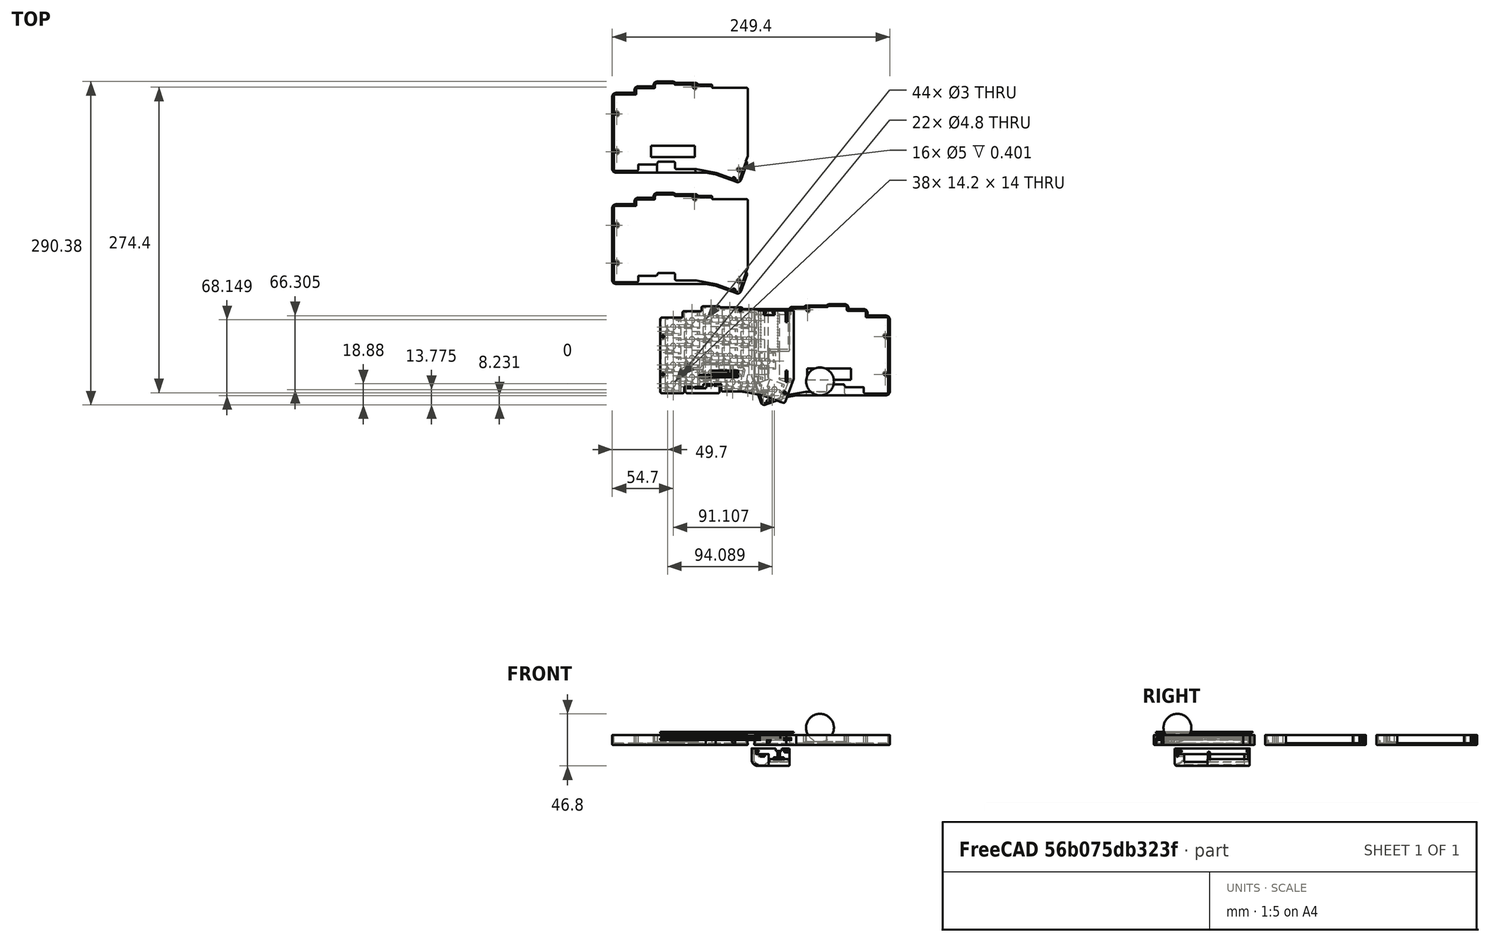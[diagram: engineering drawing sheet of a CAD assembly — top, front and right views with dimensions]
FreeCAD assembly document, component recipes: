
FREECAD ASSEMBLY — COMPONENT RECIPES ("simple-case-xs")

This assembly document has 5 components, labeled P0..P4 below (a component is one placed body or linked part). 4 of them carry a construction recipe — the FreeCAD feature program that regenerates the part from scratch, quoted from this document or its linked companion documents; the rest are supplied as boundary geometry only. No exploded tour is included for this assembly.
NOTE — document 2 of 3 of this assembly tour. The two overview renders and the header above are repeated from document 1; the component sections below continue where the previous document stopped.
COMPONENT P2 — recipe-attached ("case-key001", modeled in this document).
Construction recipe (the document's own serialized feature program — sketch geometry with constraints, then the solid features built on it; lengths are millimeters unless a unit is written):

FEATURE [Sketcher::SketchObject] Sketch020  label="top-plate"
  ArcFitTolerance = 1e-06
  FullyConstrained = true
  MakeInternals = false
  Placement = pos=(0,0,6.6e-15) rot=(0,0,1;0rad)
  sketch-geometry (128):
    g0: ArcOfCircle CenterX=45.3 CenterY=2.4 CenterZ=0 NormalX=-1e-16 NormalY=0 NormalZ=1 AngleXU=1.5708 Radius=1.5 StartAngle=0 EndAngle=1.22777
    g1: LineSegment StartX=59.4 StartY=3.9 StartZ=0 EndX=45.3 EndY=3.9 EndZ=0
    g2: LineSegment StartX=43.8874 StartY=2.9045 StartZ=0 EndX=43.8874 EndY=2.8 EndZ=0
    g3: ArcOfCircle CenterX=59.4 CenterY=2.4 CenterZ=0 NormalX=-1e-16 NormalY=0 NormalZ=1 AngleXU=3.90995e-07 Radius=1.5 StartAngle=0 EndAngle=1.5708
    g4: LineSegment StartX=60.9 StartY=-0.4 StartZ=0 EndX=60.9 EndY=2.4 EndZ=0
    g5: LineSegment StartX=76.4 StartY=-0.4 StartZ=0 EndX=60.9 EndY=-0.4 EndZ=0
    g6: ArcOfCircle CenterX=76.4 CenterY=-1.9 CenterZ=0 NormalX=-1e-16 NormalY=0 NormalZ=1 AngleXU=3.90995e-07 Radius=1.5 StartAngle=0 EndAngle=1.5708
    g7: LineSegment StartX=77.9 StartY=-6.3 StartZ=0 EndX=77.9 EndY=-1.9 EndZ=0
    g8: LineSegment StartX=96.4 StartY=-6.3 StartZ=0 EndX=77.9 EndY=-6.3 EndZ=0
    g9: ArcOfCircle CenterX=96.4 CenterY=-7.8 CenterZ=0 NormalX=-1e-16 NormalY=0 NormalZ=1 AngleXU=3.90995e-07 Radius=1.5 StartAngle=0 EndAngle=1.5708
    g10: LineSegment StartX=97.9 StartY=-59.8 StartZ=0 EndX=97.9 EndY=-7.8 EndZ=0
    g11: LineSegment StartX=97.9 StartY=-72.8 StartZ=0 EndX=97.9 EndY=-59.8 EndZ=0
    g12: ArcOfCircle CenterX=96.4 CenterY=-72.8 CenterZ=0 NormalX=-1e-16 NormalY=0 NormalZ=1 AngleXU=-1.5708 Radius=1.5 StartAngle=0 EndAngle=1.5708
    g13: LineSegment StartX=78 StartY=-74.3 StartZ=0 EndX=96.4 EndY=-74.3 EndZ=0
    g14: ArcOfCircle CenterX=78 CenterY=-72.8 CenterZ=0 NormalX=-1e-16 NormalY=0 NormalZ=1 AngleXU=-3.14159 Radius=1.5 StartAngle=0 EndAngle=1.5708
    g15: LineSegment StartX=76.5 StartY=-68.4 StartZ=0 EndX=76.5 EndY=-72.8 EndZ=0
    g16: LineSegment StartX=60.7 StartY=-68.4 StartZ=0 EndX=76.5 EndY=-68.4 EndZ=0
    g17: ArcOfCircle CenterX=60.7 CenterY=-66.9 CenterZ=0 NormalX=-1e-16 NormalY=0 NormalZ=1 AngleXU=-3.14159 Radius=1.5 StartAngle=0 EndAngle=1.5708
    g18: LineSegment StartX=59.2 StartY=-66.1 StartZ=0 EndX=59.2 EndY=-66.9 EndZ=0
    g19: LineSegment StartX=43.1 StartY=-66.1 StartZ=0 EndX=59.2 EndY=-66.1 EndZ=0
    g20: LineSegment StartX=43.1 StartY=-71.2 StartZ=0 EndX=43.1 EndY=-66.1 EndZ=0
    g21: ArcOfCircle CenterX=41.6 CenterY=-71.2 CenterZ=0 NormalX=-1e-16 NormalY=0 NormalZ=1 AngleXU=-1.5708 Radius=1.5 StartAngle=0 EndAngle=1.5708
    g22: LineSegment StartX=41.4 StartY=-72.7 StartZ=0 EndX=41.6 EndY=-72.7 EndZ=0
    g23: LineSegment StartX=24.227 StartY=-72.7043 StartZ=0 EndX=41.4 EndY=-72.7 EndZ=0
    g24: LineSegment StartX=6.18739 StartY=-75.9853 StartZ=0 EndX=24.227 EndY=-72.7043 EndZ=0
    g25: LineSegment StartX=-12.4977 StartY=-82.7894 StartZ=0 EndX=6.18739 EndY=-75.9853 EndZ=0
    g26: ArcOfCircle CenterX=-13.0109 CenterY=-81.3798 CenterZ=0 NormalX=-1e-16 NormalY=0 NormalZ=1 AngleXU=-2.78723 Radius=1.50005 StartAngle=0 EndAngle=1.56562
    g27: LineSegment StartX=-20.3 StartY=-66 StartZ=0 EndX=-14.4178 EndY=-81.9004 EndZ=0
    g28: LineSegment StartX=-9.1 StartY=-61.9235 StartZ=0 EndX=-20.3 EndY=-66 EndZ=0
    g29: LineSegment StartX=-9.1 StartY=-61 StartZ=0 EndX=-9.1 EndY=-61.9235 EndZ=0
    g30: LineSegment StartX=-9.1 StartY=-36.9 StartZ=0 EndX=-9.1 EndY=-61 EndZ=0
    g31: LineSegment StartX=9.9 StartY=-36.9 StartZ=0 EndX=-9.1 EndY=-36.9 EndZ=0
    g32: LineSegment StartX=9.9 StartY=1.3 StartZ=0 EndX=9.9 EndY=-36.9 EndZ=0
    g33: LineSegment StartX=23.7 StartY=1.3 StartZ=0 EndX=9.9 EndY=1.3 EndZ=0
    g34: ArcOfCircle CenterX=25.2 CenterY=1.3 CenterZ=0 NormalX=-1e-16 NormalY=0 NormalZ=1 AngleXU=1.5708 Radius=1.5 StartAngle=0 EndAngle=1.5708
    g35: LineSegment StartX=43.8874 StartY=2.8 StartZ=0 EndX=25.2 EndY=2.8 EndZ=0
    g36: LineSegment StartX=93.5 StartY=-72.8 StartZ=0 EndX=79.3 EndY=-72.8 EndZ=0
    g37: LineSegment StartX=93.5 StartY=-58.8 StartZ=0 EndX=93.5 EndY=-72.8 EndZ=0
    g38: LineSegment StartX=79.3 StartY=-58.8 StartZ=0 EndX=93.5 EndY=-58.8 EndZ=0
    g39: LineSegment StartX=79.3 StartY=-72.8 StartZ=0 EndX=79.3 EndY=-58.8 EndZ=0
    g40: LineSegment StartX=76.5 StartY=-66.85 StartZ=0 EndX=62.3 EndY=-66.85 EndZ=0
    g41: LineSegment StartX=76.5 StartY=-52.85 StartZ=0 EndX=76.5 EndY=-66.85 EndZ=0
    g42: LineSegment StartX=62.3 StartY=-52.85 StartZ=0 EndX=76.5 EndY=-52.85 EndZ=0
    g43: LineSegment StartX=62.3 StartY=-66.85 StartZ=0 EndX=62.3 EndY=-52.85 EndZ=0
    g44: Circle CenterX=95.6 CenterY=-57.3 CenterZ=0 NormalX=-1e-16 NormalY=0 NormalZ=1 AngleXU=-1.5708 Radius=1.1
    g45: LineSegment StartX=93.5 StartY=-55.8 StartZ=0 EndX=79.3 EndY=-55.8 EndZ=0
    g46: LineSegment StartX=93.5 StartY=-41.8 StartZ=0 EndX=93.5 EndY=-55.8 EndZ=0
    g47: LineSegment StartX=79.3 StartY=-41.8 StartZ=0 EndX=93.5 EndY=-41.8 EndZ=0
    g48: LineSegment StartX=79.3 StartY=-55.8 StartZ=0 EndX=79.3 EndY=-41.8 EndZ=0
    g49: LineSegment StartX=76.5 StartY=-49.85 StartZ=0 EndX=62.3 EndY=-49.85 EndZ=0
    g50: LineSegment StartX=76.5 StartY=-35.85 StartZ=0 EndX=76.5 EndY=-49.85 EndZ=0
    g51: LineSegment StartX=62.3 StartY=-35.85 StartZ=0 EndX=76.5 EndY=-35.85 EndZ=0
    g52: LineSegment StartX=62.3 StartY=-49.85 StartZ=0 EndX=62.3 EndY=-35.85 EndZ=0
    g53: LineSegment StartX=59.5 StartY=-62.6 StartZ=0 EndX=45.3 EndY=-62.6 EndZ=0
    g54: LineSegment StartX=59.5 StartY=-48.6 StartZ=0 EndX=59.5 EndY=-62.6 EndZ=0
    g55: LineSegment StartX=45.3 StartY=-48.6 StartZ=0 EndX=59.5 EndY=-48.6 EndZ=0
    g56: LineSegment StartX=45.3 StartY=-62.6 StartZ=0 EndX=45.3 EndY=-48.6 EndZ=0
    g57: LineSegment StartX=39.95 StartY=-71.1 StartZ=0 EndX=25.75 EndY=-71.1 EndZ=0
    g58: LineSegment StartX=39.95 StartY=-57.1 StartZ=0 EndX=39.95 EndY=-71.1 EndZ=0
    g59: LineSegment StartX=25.75 StartY=-57.1 StartZ=0 EndX=39.95 EndY=-57.1 EndZ=0
    g60: LineSegment StartX=25.75 StartY=-71.1 StartZ=0 EndX=25.75 EndY=-57.1 EndZ=0
    g61: LineSegment StartX=21.8608 StartY=-71.3659 StartZ=0 EndX=7.87653 EndY=-73.8317 EndZ=0
    g62: LineSegment StartX=19.4297 StartY=-57.5786 StartZ=0 EndX=21.8608 EndY=-71.3659 EndZ=0
    g63: LineSegment StartX=5.44545 StartY=-60.0444 StartZ=0 EndX=19.4297 EndY=-57.5786 EndZ=0
    g64: LineSegment StartX=7.87653 StartY=-73.8317 StartZ=0 EndX=5.44545 EndY=-60.0444 EndZ=0
    g65: LineSegment StartX=4.35879 StartY=-75.0546 StartZ=0 EndX=-8.98485 EndY=-79.9113 EndZ=0
    g66: LineSegment StartX=-0.429495 StartY=-61.8989 StartZ=0 EndX=4.35879 EndY=-75.0546 EndZ=0
    g67: LineSegment StartX=-13.7731 StartY=-66.7556 StartZ=0 EndX=-0.429495 EndY=-61.8989 EndZ=0
    g68: LineSegment StartX=-8.98485 StartY=-79.9113 StartZ=0 EndX=-13.7731 EndY=-66.7556 EndZ=0
    g69: Circle CenterX=-14 CenterY=-73.8 CenterZ=0 NormalX=-1e-16 NormalY=0 NormalZ=1 AngleXU=-1.5708 Radius=1.1
    g70: LineSegment StartX=42.5 StartY=-47.725 StartZ=0 EndX=28.3 EndY=-47.725 EndZ=0
    g71: LineSegment StartX=42.5 StartY=-33.725 StartZ=0 EndX=42.5 EndY=-47.725 EndZ=0
    g72: LineSegment StartX=28.3 StartY=-33.725 StartZ=0 EndX=42.5 EndY=-33.725 EndZ=0
    g73: LineSegment StartX=28.3 StartY=-47.725 StartZ=0 EndX=28.3 EndY=-33.725 EndZ=0
    g74: LineSegment StartX=25.5 StartY=-49.85 StartZ=0 EndX=11.3 EndY=-49.85 EndZ=0
    g75: LineSegment StartX=25.5 StartY=-35.85 StartZ=0 EndX=25.5 EndY=-49.85 EndZ=0
    g76: LineSegment StartX=11.3 StartY=-35.85 StartZ=0 EndX=25.5 EndY=-35.85 EndZ=0
    g77: LineSegment StartX=11.3 StartY=-49.85 StartZ=0 EndX=11.3 EndY=-35.85 EndZ=0
    g78: LineSegment StartX=8.5 StartY=-52.4 StartZ=0 EndX=-5.7 EndY=-52.4 EndZ=0
    g79: LineSegment StartX=8.5 StartY=-38.4 StartZ=0 EndX=8.5 EndY=-52.4 EndZ=0
    g80: LineSegment StartX=-5.7 StartY=-38.4 StartZ=0 EndX=8.5 EndY=-38.4 EndZ=0
    g81: LineSegment StartX=-5.7 StartY=-52.4 StartZ=0 EndX=-5.7 EndY=-38.4 EndZ=0
    g82: LineSegment StartX=93.5 StartY=-38.8 StartZ=0 EndX=79.3 EndY=-38.8 EndZ=0
    g83: LineSegment StartX=93.5 StartY=-24.8 StartZ=0 EndX=93.5 EndY=-38.8 EndZ=0
    g84: LineSegment StartX=79.3 StartY=-24.8 StartZ=0 EndX=93.5 EndY=-24.8 EndZ=0
    g85: LineSegment StartX=79.3 StartY=-38.8 StartZ=0 EndX=79.3 EndY=-24.8 EndZ=0
    g86: Circle CenterX=95.6 CenterY=-23.3 CenterZ=0 NormalX=-1e-16 NormalY=0 NormalZ=1 AngleXU=-1.5708 Radius=1.1
    g87: LineSegment StartX=76.5 StartY=-32.85 StartZ=0 EndX=62.3 EndY=-32.85 EndZ=0
    g88: LineSegment StartX=76.5 StartY=-18.85 StartZ=0 EndX=76.5 EndY=-32.85 EndZ=0
    g89: LineSegment StartX=62.3 StartY=-18.85 StartZ=0 EndX=76.5 EndY=-18.85 EndZ=0
    g90: LineSegment StartX=62.3 StartY=-32.85 StartZ=0 EndX=62.3 EndY=-18.85 EndZ=0
    g91: LineSegment StartX=59.5 StartY=-45.6 StartZ=0 EndX=45.3 EndY=-45.6 EndZ=0
    g92: LineSegment StartX=59.5 StartY=-31.6 StartZ=0 EndX=59.5 EndY=-45.6 EndZ=0
    g93: LineSegment StartX=45.3 StartY=-31.6 StartZ=0 EndX=59.5 EndY=-31.6 EndZ=0
    g94: LineSegment StartX=45.3 StartY=-45.6 StartZ=0 EndX=45.3 EndY=-31.6 EndZ=0
    g95: LineSegment StartX=59.5 StartY=-28.6 StartZ=0 EndX=45.3 EndY=-28.6 EndZ=0
    g96: LineSegment StartX=59.5 StartY=-14.6 StartZ=0 EndX=59.5 EndY=-28.6 EndZ=0
    g97: LineSegment StartX=45.3 StartY=-14.6 StartZ=0 EndX=59.5 EndY=-14.6 EndZ=0
    g98: LineSegment StartX=45.3 StartY=-28.6 StartZ=0 EndX=45.3 EndY=-14.6 EndZ=0
    g99: LineSegment StartX=93.5 StartY=-21.8 StartZ=0 EndX=79.3 EndY=-21.8 EndZ=0
    g100: LineSegment StartX=93.5 StartY=-7.8 StartZ=0 EndX=93.5 EndY=-21.8 EndZ=0
    g101: LineSegment StartX=79.3 StartY=-7.8 StartZ=0 EndX=93.5 EndY=-7.8 EndZ=0
    g102: LineSegment StartX=79.3 StartY=-21.8 StartZ=0 EndX=79.3 EndY=-7.8 EndZ=0
    g103: LineSegment StartX=76.5 StartY=-15.85 StartZ=0 EndX=62.3 EndY=-15.85 EndZ=0
    g104: LineSegment StartX=76.5 StartY=-1.85 StartZ=0 EndX=76.5 EndY=-15.85 EndZ=0
    g105: LineSegment StartX=62.3 StartY=-1.85 StartZ=0 EndX=76.5 EndY=-1.85 EndZ=0
    g106: LineSegment StartX=62.3 StartY=-15.85 StartZ=0 EndX=62.3 EndY=-1.85 EndZ=0
    g107: LineSegment StartX=59.5 StartY=-11.6 StartZ=0 EndX=45.3 EndY=-11.6 EndZ=0
    g108: LineSegment StartX=59.5 StartY=2.4 StartZ=0 EndX=59.5 EndY=-11.6 EndZ=0
    g109: LineSegment StartX=45.3 StartY=2.4 StartZ=0 EndX=59.5 EndY=2.4 EndZ=0
    g110: LineSegment StartX=45.3 StartY=-11.6 StartZ=0 EndX=45.3 EndY=2.4 EndZ=0
    g111: LineSegment StartX=42.5 StartY=-30.725 StartZ=0 EndX=28.3 EndY=-30.725 EndZ=0
    g112: LineSegment StartX=42.5 StartY=-16.725 StartZ=0 EndX=42.5 EndY=-30.725 EndZ=0
    g113: LineSegment StartX=28.3 StartY=-16.725 StartZ=0 EndX=42.5 EndY=-16.725 EndZ=0
    g114: LineSegment StartX=28.3 StartY=-30.725 StartZ=0 EndX=28.3 EndY=-16.725 EndZ=0
    g115: LineSegment StartX=25.5 StartY=-32.85 StartZ=0 EndX=11.3 EndY=-32.85 EndZ=0
    g116: LineSegment StartX=25.5 StartY=-18.85 StartZ=0 EndX=25.5 EndY=-32.85 EndZ=0
    g117: LineSegment StartX=11.3 StartY=-18.85 StartZ=0 EndX=25.5 EndY=-18.85 EndZ=0
    g118: LineSegment StartX=11.3 StartY=-32.85 StartZ=0 EndX=11.3 EndY=-18.85 EndZ=0
    g119: LineSegment StartX=25.5 StartY=-15.85 StartZ=0 EndX=11.3 EndY=-15.85 EndZ=0
    g120: LineSegment StartX=25.5 StartY=-1.85 StartZ=0 EndX=25.5 EndY=-15.85 EndZ=0
    g121: LineSegment StartX=11.3 StartY=-1.85 StartZ=0 EndX=25.5 EndY=-1.85 EndZ=0
    g122: LineSegment StartX=11.3 StartY=-15.85 StartZ=0 EndX=11.3 EndY=-1.85 EndZ=0
    g123: LineSegment StartX=42.5 StartY=-13.725 StartZ=0 EndX=28.3 EndY=-13.725 EndZ=0
    g124: LineSegment StartX=42.5 StartY=0.275 StartZ=0 EndX=42.5 EndY=-13.725 EndZ=0
    g125: LineSegment StartX=28.3 StartY=0.275 StartZ=0 EndX=42.5 EndY=0.275 EndZ=0
    g126: LineSegment StartX=28.3 StartY=-13.725 StartZ=0 EndX=28.3 EndY=0.275 EndZ=0
    g127: Circle CenterX=25.9 CenterY=0.6 CenterZ=0 NormalX=-1e-16 NormalY=0 NormalZ=1 AngleXU=-1.5708 Radius=1.1
  constraints (252):
    c: Block(g0)
    c: Block(g1)
    c: Block(g2)
    c: Block(g3)
    c: Block(g4)
    c: Block(g5)
    c: Block(g6)
    c: Block(g7)
    c: Block(g8)
    c: Block(g9)
    c: Block(g10)
    c: Block(g11)
    c: Block(g12)
    c: Block(g13)
    c: Block(g14)
    c: Block(g15)
    c: Block(g16)
    c: Block(g17)
    c: Block(g18)
    c: Block(g19)
    c: Block(g20)
    c: Block(g21)
    c: Block(g22)
    c: Block(g23)
    c: Block(g24)
    c: Block(g25)
    c: Block(g26)
    c: Block(g27)
    c: Block(g28)
    c: Block(g29)
    c: Block(g30)
    c: Block(g31)
    c: Block(g32)
    c: Block(g33)
    c: Block(g34)
    c: Block(g35)
    c: Block(g36)
    c: Block(g37)
    c: Block(g38)
    c: Block(g39)
    c: Block(g40)
    c: Block(g41)
    c: Block(g42)
    c: Block(g43)
    c: Block(g44)
    c: Block(g45)
    c: Block(g46)
    c: Block(g47)
    c: Block(g48)
    c: Block(g49)
    c: Block(g50)
    c: Block(g51)
    c: Block(g52)
    c: Block(g53)
    c: Block(g54)
    c: Block(g55)
    c: Block(g56)
    c: Block(g57)
    c: Block(g58)
    c: Block(g59)
    c: Block(g60)
    c: Block(g61)
    c: Block(g62)
    c: Block(g63)
    c: Block(g64)
    c: Block(g65)
    c: Block(g66)
    c: Block(g67)
    c: Block(g68)
    c: Block(g69)
    c: Block(g70)
    c: Block(g71)
    c: Block(g72)
    c: Block(g73)
    c: Block(g74)
    c: Block(g75)
    c: Block(g76)
    c: Block(g77)
    c: Block(g78)
    c: Block(g79)
    c: Block(g80)
    c: Block(g81)
    c: Block(g82)
    c: Block(g83)
    c: Block(g84)
    c: Block(g85)
    c: Block(g86)
    c: Block(g87)
    c: Block(g88)
    c: Block(g89)
    c: Block(g90)
    c: Block(g91)
    c: Block(g92)
    c: Block(g93)
    c: Block(g94)
    c: Block(g95)
    c: Block(g96)
    c: Block(g97)
    c: Block(g98)
    c: Block(g99)
    c: Block(g100)
    c: Block(g101)
    c: Block(g102)
    c: Block(g103)
    c: Block(g104)
    c: Block(g105)
    c: Block(g106)
    c: Block(g107)
    c: Block(g108)
    c: Block(g109)
    c: Block(g110)
    c: Block(g111)
    c: Block(g112)
    c: Block(g113)
    c: Block(g114)
    c: Block(g115)
    c: Block(g116)
    c: Block(g117)
    c: Block(g118)
    c: Block(g119)
    c: Block(g120)
    c: Block(g121)
    c: Block(g122)
    c: Block(g123)
    c: Block(g124)
    c: Block(g125)
    c: Block(g126)
    c: Block(g127)
    c: Coincident(g27,g28)
    c: Coincident(g26,g27)
    c: Coincident(g67,g68)
    c: Coincident(g25,g26)
    c: Coincident(g28,g29)
    c: Coincident(g29,g30)
    c: Coincident(g30,g31)
    c: Coincident(g65,g68)
    c: Coincident(g78,g81)
    c: Coincident(g80,g81)
    c: Coincident(g66,g67)
    c: Coincident(g65,g66)
    c: Coincident(g63,g64)
    c: Coincident(g24,g25)
    c: Coincident(g61,g64)
    c: Coincident(g78,g79)
    c: Coincident(g79,g80)
    c: Coincident(g31,g32)
    c: Coincident(g32,g33)
    c: Coincident(g74,g77)
    c: Coincident(g76,g77)
    c: Coincident(g115,g118)
    c: Coincident(g117,g118)
    c: Coincident(g119,g122)
    c: Coincident(g121,g122)
    c: Coincident(g62,g63)
    c: Coincident(g61,g62)
    c: Coincident(g33,g34)
    c: Coincident(g23,g24)
    c: Coincident(g34,g35)
    c: Coincident(g74,g75)
    c: Coincident(g75,g76)
    c: Coincident(g115,g116)
    c: Coincident(g116,g117)
    c: Coincident(g119,g120)
    c: Coincident(g120,g121)
    c: Coincident(g57,g60)
    c: Coincident(g59,g60)
    c: Coincident(g70,g73)
    c: Coincident(g72,g73)
    c: Coincident(g111,g114)
    c: Coincident(g113,g114)
    c: Coincident(g123,g126)
    c: Coincident(g125,g126)
    c: Coincident(g57,g58)
    c: Coincident(g58,g59)
    c: Coincident(g22,g23)
    c: Coincident(g21,g22)
    c: Coincident(g70,g71)
    c: Coincident(g71,g72)
    c: Coincident(g111,g112)
    c: Coincident(g112,g113)
    c: Coincident(g123,g124)
    c: Coincident(g124,g125)
    c: Coincident(g20,g21)
    c: Coincident(g19,g20)
    c: Coincident(g2,g35)
    c: Coincident(g0,g2)
    c: Coincident(g53,g56)
    c: Coincident(g55,g56)
    c: Coincident(g91,g94)
    c: Coincident(g93,g94)
    c: Coincident(g95,g98)
    c: Coincident(g97,g98)
    c: Coincident(g107,g110)
    c: Coincident(g109,g110)
    c: Coincident(g0,g1)
    c: Coincident(g17,g18)
    c: Coincident(g18,g19)
    c: Coincident(g1,g3)
    c: Coincident(g53,g54)
    c: Coincident(g54,g55)
    c: Coincident(g91,g92)
    c: Coincident(g92,g93)
    c: Coincident(g95,g96)
    c: Coincident(g96,g97)
    c: Coincident(g107,g108)
    c: Coincident(g108,g109)
    c: Coincident(g16,g17)
    c: Coincident(g4,g5)
    c: Coincident(g3,g4)
    c: Coincident(g40,g43)
    c: Coincident(g42,g43)
    c: Coincident(g49,g52)
    c: Coincident(g51,g52)
    c: Coincident(g87,g90)
    c: Coincident(g89,g90)
    c: Coincident(g103,g106)
    c: Coincident(g105,g106)
    c: Coincident(g5,g6)
    c: Coincident(g14,g15)
    c: Coincident(g15,g16)
    c: Coincident(g40,g41)
    c: Coincident(g41,g42)
    c: Coincident(g49,g50)
    c: Coincident(g50,g51)
    c: Coincident(g87,g88)
    c: Coincident(g88,g89)
    c: Coincident(g103,g104)
    c: Coincident(g104,g105)
    c: Coincident(g7,g8)
    c: Coincident(g6,g7)
    c: Coincident(g13,g14)
    c: Coincident(g36,g39)
    c: Coincident(g38,g39)
    c: Coincident(g45,g48)
    c: Coincident(g47,g48)
    c: Coincident(g82,g85)
    c: Coincident(g84,g85)
    c: Coincident(g99,g102)
    c: Coincident(g101,g102)
    c: Coincident(g36,g37)
    c: Coincident(g37,g38)
    c: Coincident(g45,g46)
    c: Coincident(g46,g47)
    c: Coincident(g82,g83)
    c: Coincident(g83,g84)
    c: Coincident(g99,g100)
    c: Coincident(g100,g101)
    c: Coincident(g12,g13)
    c: Coincident(g8,g9)
    c: Coincident(g11,g12)
    c: Coincident(g10,g11)
    c: Coincident(g9,g10)
FEATURE [Sketcher::SketchObject] Sketch021
  ArcFitTolerance = 1e-06
  AttachmentOffset = pos=(0,0,-5.1) rot=(0,0,1;0rad)
  AttachmentSupport = -> [XY_Plane004]
  FullyConstrained = false
  MakeInternals = false
  MapMode = 5
  Placement = pos=(0,0,-5.1) rot=(0,0,1;0rad)
  sketch-geometry (61):
    g0: ArcOfCircle [constr] CenterX=45.3 CenterY=2.4 CenterZ=0 NormalX=-1e-16 NormalY=0 NormalZ=1 AngleXU=1.5708 Radius=1.5 StartAngle=0 EndAngle=1.22777
    g1: LineSegment [constr] StartX=59.4 StartY=3.9 StartZ=0 EndX=45.3 EndY=3.9 EndZ=0
    g2: LineSegment [constr] StartX=43.8874 StartY=2.9045 StartZ=0 EndX=43.8874 EndY=2.8 EndZ=0
    g3: ArcOfCircle [constr] CenterX=59.4 CenterY=2.4 CenterZ=0 NormalX=-1e-16 NormalY=0 NormalZ=1 AngleXU=3.90995e-07 Radius=1.5 StartAngle=0 EndAngle=1.5708
    g4: LineSegment [constr] StartX=60.9 StartY=-0.4 StartZ=0 EndX=60.9 EndY=2.4 EndZ=0
    g5: LineSegment [constr] StartX=76.4 StartY=-0.4 StartZ=0 EndX=60.9 EndY=-0.4 EndZ=0
    g6: ArcOfCircle [constr] CenterX=76.4 CenterY=-1.9 CenterZ=0 NormalX=-1e-16 NormalY=0 NormalZ=1 AngleXU=3.90995e-07 Radius=1.5 StartAngle=0 EndAngle=1.5708
    g7: LineSegment [constr] StartX=77.9 StartY=-6.3 StartZ=0 EndX=77.9 EndY=-1.9 EndZ=0
    g8: LineSegment [constr] StartX=96.4 StartY=-6.3 StartZ=0 EndX=77.9 EndY=-6.3 EndZ=0
    g9: ArcOfCircle [constr] CenterX=96.4 CenterY=-7.8 CenterZ=0 NormalX=-1e-16 NormalY=0 NormalZ=1 AngleXU=3.90995e-07 Radius=1.5 StartAngle=0 EndAngle=1.5708
    g10: LineSegment [constr] StartX=97.9 StartY=-59.8 StartZ=0 EndX=97.9 EndY=-7.8 EndZ=0
    g11: LineSegment [constr] StartX=97.9 StartY=-72.8 StartZ=0 EndX=97.9 EndY=-59.8 EndZ=0
    g12: ArcOfCircle [constr] CenterX=96.4 CenterY=-72.8 CenterZ=0 NormalX=-1e-16 NormalY=0 NormalZ=1 AngleXU=-1.5708 Radius=1.5 StartAngle=0 EndAngle=1.5708
    g13: LineSegment [constr] StartX=78 StartY=-74.3 StartZ=0 EndX=96.4 EndY=-74.3 EndZ=0
    g14: LineSegment [constr] StartX=6.18739 StartY=-75.9853 StartZ=0 EndX=15.4535 EndY=-74.3 EndZ=0
    g15: LineSegment [constr] StartX=-12.4977 StartY=-82.7894 StartZ=0 EndX=6.18739 EndY=-75.9853 EndZ=0
    g16: ArcOfCircle [constr] CenterX=-13.0109 CenterY=-81.3798 CenterZ=0 NormalX=-1e-16 NormalY=0 NormalZ=1 AngleXU=-2.78723 Radius=1.50005 StartAngle=0 EndAngle=1.56562
    g17: LineSegment [constr] StartX=-20.3 StartY=-66 StartZ=0 EndX=-14.4178 EndY=-81.9004 EndZ=0
    g18: LineSegment [constr] StartX=-9.1 StartY=-61.9235 StartZ=0 EndX=-20.3 EndY=-66 EndZ=0
    g19: LineSegment [constr] StartX=-9.1 StartY=-61 StartZ=0 EndX=-9.1 EndY=-61.9235 EndZ=0
    g20: LineSegment [constr] StartX=-9.1 StartY=-36.9 StartZ=0 EndX=-9.1 EndY=-61 EndZ=0
    g21: LineSegment [constr] StartX=9.9 StartY=-36.9 StartZ=0 EndX=-9.1 EndY=-36.9 EndZ=0
    g22: LineSegment [constr] StartX=9.9 StartY=1.3 StartZ=0 EndX=9.9 EndY=-36.9 EndZ=0
    g23: LineSegment [constr] StartX=23.7 StartY=1.3 StartZ=0 EndX=9.9 EndY=1.3 EndZ=0
    g24: ArcOfCircle [constr] CenterX=25.2 CenterY=1.3 CenterZ=0 NormalX=-1e-16 NormalY=0 NormalZ=1 AngleXU=1.5708 Radius=1.5 StartAngle=0 EndAngle=1.5708
    g25: LineSegment [constr] StartX=43.8874 StartY=2.8 StartZ=0 EndX=25.2 EndY=2.8 EndZ=0
    g26: LineSegment [constr] StartX=78 StartY=-74.3 StartZ=0 EndX=15.4535 EndY=-74.3 EndZ=0
    g27: LineSegment StartX=78 StartY=-76.1 StartZ=0 EndX=15.6159 EndY=-76.1 EndZ=0
    g28: LineSegment StartX=6.65976 StartY=-77.7289 StartZ=0 EndX=15.6159 EndY=-76.1 EndZ=0
    g29: LineSegment StartX=-11.8818 StartY=-84.4807 StartZ=0 EndX=6.65976 EndY=-77.7289 EndZ=0
    g30: ArcOfCircle CenterX=-13.0109 CenterY=-81.3798 CenterZ=0 NormalX=0 NormalY=0 NormalZ=1 AngleXU=-2.78723 Radius=3.30007 StartAngle=6.28318 EndAngle=7.84881
    g31: LineSegment StartX=-21.9882 StartY=-66.6245 StartZ=0 EndX=-16.106 EndY=-82.5249 EndZ=0
    g32: LineSegment [constr] StartX=-10.9 StartY=-60.6632 StartZ=0 EndX=-20.9156 EndY=-64.3086 EndZ=0
    g33: LineSegment [constr] StartX=-10.9 StartY=-36.9 StartZ=0 EndX=-10.9 EndY=-60.6632 EndZ=0
    g34: ArcOfCircle [constr] CenterX=-9.1 CenterY=-36.9 CenterZ=0 NormalX=0 NormalY=0 NormalZ=1 AngleXU=0 Radius=1.8 StartAngle=1.5708 EndAngle=3.14159
    g35: LineSegment [constr] StartX=8.1 StartY=-35.1 StartZ=0 EndX=-9.1 EndY=-35.1 EndZ=0
    g36: LineSegment [constr] StartX=8.1 StartY=1.3 StartZ=0 EndX=8.1 EndY=-35.1 EndZ=0
    g37: ArcOfCircle [constr] CenterX=9.9 CenterY=1.3 CenterZ=0 NormalX=0 NormalY=0 NormalZ=1 AngleXU=0 Radius=1.8 StartAngle=1.5708 EndAngle=3.14159
    g38: LineSegment [constr] StartX=22.4341 StartY=3.1 StartZ=0 EndX=9.9 EndY=3.1 EndZ=0
    g39: ArcOfCircle CenterX=25.2 CenterY=1.3 CenterZ=0 NormalX=0 NormalY=0 NormalZ=1 AngleXU=1.5708 Radius=3.3 StartAngle=0 EndAngle=0.993864
    g40: LineSegment StartX=42.8403 StartY=4.6 StartZ=0 EndX=25.2 EndY=4.6 EndZ=0
    g41: ArcOfCircle CenterX=45.3 CenterY=2.4 CenterZ=0 NormalX=0 NormalY=0 NormalZ=1 AngleXU=1.5708 Radius=3.3 StartAngle=0 EndAngle=0.841069
    g42: LineSegment StartX=59.4 StartY=5.7 StartZ=0 EndX=45.3 EndY=5.7 EndZ=0
    g43: ArcOfCircle CenterX=59.4 CenterY=2.4 CenterZ=0 NormalX=0 NormalY=0 NormalZ=1 AngleXU=3.90995e-07 Radius=3.3 StartAngle=-1.8e-15 EndAngle=1.5708
    g44: LineSegment StartX=62.7 StartY=1.4 StartZ=0 EndX=62.7 EndY=2.4 EndZ=0
    g45: LineSegment StartX=76.4 StartY=1.4 StartZ=0 EndX=62.7 EndY=1.4 EndZ=0
    g46: ArcOfCircle CenterX=76.4 CenterY=-1.9 CenterZ=0 NormalX=0 NormalY=0 NormalZ=1 AngleXU=3.90995e-07 Radius=3.3 StartAngle=-1.8e-15 EndAngle=1.5708
    g47: LineSegment StartX=79.7 StartY=-4.5 StartZ=0 EndX=79.7 EndY=-1.9 EndZ=0
    g48: LineSegment StartX=96.4 StartY=-4.5 StartZ=0 EndX=79.7 EndY=-4.5 EndZ=0
    g49: ArcOfCircle CenterX=96.4 CenterY=-7.8 CenterZ=0 NormalX=0 NormalY=0 NormalZ=1 AngleXU=3.90995e-07 Radius=3.3 StartAngle=-1.8e-15 EndAngle=1.5708
    g50: LineSegment StartX=99.7 StartY=-59.8 StartZ=0 EndX=99.7 EndY=-7.8 EndZ=0
    g51: LineSegment StartX=99.7 StartY=-72.8 StartZ=0 EndX=99.7 EndY=-59.8 EndZ=0
    g52: ArcOfCircle CenterX=96.4 CenterY=-72.8 CenterZ=0 NormalX=0 NormalY=0 NormalZ=1 AngleXU=-1.5708 Radius=3.3 StartAngle=0 EndAngle=1.5708
    g53: LineSegment StartX=78 StartY=-76.1 StartZ=0 EndX=96.4 EndY=-76.1 EndZ=0
    g54: LineSegment [constr] StartX=8.1 StartY=1.3 StartZ=0 EndX=8.1 EndY=0 EndZ=0
    g55: LineSegment StartX=8.1 StartY=0 StartZ=0 EndX=-22.1 EndY=0 EndZ=0
    g56: LineSegment StartX=-22.1 StartY=0 StartZ=0 EndX=-22.1 EndY=-61.0545 EndZ=0
    g57: LineSegment StartX=-22.1 StartY=-61.0545 StartZ=0 EndX=-20.3 EndY=-66 EndZ=0
    g58: LineSegment StartX=-20.3 StartY=-66 StartZ=0 EndX=-21.9882 EndY=-66.6245 EndZ=0
    g59: LineSegment StartX=22.4341 StartY=3.1 StartZ=0 EndX=8.1 EndY=3.1 EndZ=0
    g60: LineSegment StartX=8.1 StartY=3.1 StartZ=0 EndX=8.1 EndY=0 EndZ=0
  constraints (101):
    c: Block(g0)
    c: Block(g1)
    c: Block(g2)
    c: Block(g3)
    c: Block(g4)
    c: Block(g5)
    c: Block(g6)
    c: Block(g7)
    c: Block(g8)
    c: Block(g9)
    c: Block(g10)
    c: Block(g11)
    c: Block(g12)
    c: Block(g13)
    c: Block(g14)
    c: Block(g15)
    c: Block(g16)
    c: Block(g17)
    c: Block(g18)
    c: Block(g19)
    c: Block(g20)
    c: Block(g21)
    c: Block(g22)
    c: Block(g23)
    c: Block(g24)
    c: Block(g25)
    c: Coincident(g17,g18)
    c: Coincident(g16,g17)
    c: Coincident(g15,g16)
    c: Coincident(g18,g19)
    c: Coincident(g19,g20)
    c: Coincident(g20,g21)
    c: Coincident(g14,g15)
    c: Coincident(g21,g22)
    c: Coincident(g22,g23)
    c: Coincident(g23,g24)
    c: Coincident(g24,g25)
    c: Coincident(g2,g25)
    c: Coincident(g0,g2)
    c: Coincident(g0,g1)
    c: Coincident(g1,g3)
    c: Coincident(g4,g5)
    c: Coincident(g3,g4)
    c: Coincident(g5,g6)
    c: Coincident(g7,g8)
    c: Coincident(g6,g7)
    c: Coincident(g12,g13)
    c: Coincident(g8,g9)
    c: Coincident(g11,g12)
    c: Coincident(g10,g11)
    c: Coincident(g9,g10)
    c: Coincident(g26,g13)
    c: Horizontal(g26)
    c: Coincident(g14,g26)
    c: Coincident(g27,g28)
    c: Coincident(g27,g53)
    c: Coincident(g28,g29)
    c: Coincident(g32,g33)
    c: Tangent(g33,g34) = -1.5708
    c: Tangent(g34,g35) = -1.5708
    c: Coincident(g35,g36)
    c: Tangent(g36,g37) = -1.5708
    c: Tangent(g37,g38) = -1.5708
    c: Coincident(g38,g39)
    c: Coincident(g40,g41)
    c: Coincident(g44,g45)
    c: Coincident(g47,g48)
    c: Coincident(g50,g51)
    c: Coincident(g54,g36)
    c: PointOnObject(g54,g-1)
    c: Vertical(g54)
    c: Coincident(g55,g54)
    c: PointOnObject(g55,g-1)
    c: Coincident(g56,g55)
    c: Vertical(g56)
    c: DistanceX(g55,g-1) = 22.1
    c: Coincident(g57,g56)
    c: Coincident(g57,g17)
    c: Angle(g18,g57) = 1.5708
    c: Coincident(g58,g17)
    c: Coincident(g58,g31)
    c: Coincident(g30,g31)
    c: Coincident(g29,g30)
    c: Coincident(g39,g40)
    c: Coincident(g41,g42)
    c: Coincident(g42,g43)
    c: Coincident(g43,g44)
    c: Coincident(g45,g46)
    c: Coincident(g46,g47)
    c: Coincident(g52,g53)
    c: Coincident(g48,g49)
    c: Coincident(g51,g52)
    c: Coincident(g49,g50)
    c: Block(g38)
    c: Block(g36)
    c: Coincident(g59,g38)
    c: Horizontal(g59)
    c: Tangent(g59,g37)
    c: Coincident(g60,g59)
    c: Coincident(g60,g54)
    c: Vertical(g60)
FEATURE [PartDesign::Pad] Pad010
  Direction = (0,0,1)
  Length = 7.3
  Length2 = 1.5
  Profile = -> Sketch021
  ReferenceAxis = -> Sketch021 [N_Axis]
  Refine = true
  Suppressed = false
  Type = 4
FEATURE [Sketcher::SketchObject] Sketch022  label="bottom-plate"
  ArcFitTolerance = 1e-06
  FullyConstrained = true
  MakeInternals = false
  Placement = pos=(0,0,6.6e-15) rot=(0,0,1;0rad)
  sketch-geometry (74):
    g0: ArcOfCircle CenterX=45.3 CenterY=2.4 CenterZ=0 NormalX=-1e-16 NormalY=0 NormalZ=1 AngleXU=1.5708 Radius=1.5 StartAngle=0 EndAngle=1.22777
    g1: LineSegment StartX=59.4 StartY=3.9 StartZ=0 EndX=45.3 EndY=3.9 EndZ=0
    g2: LineSegment StartX=43.8874 StartY=2.9045 StartZ=0 EndX=43.8874 EndY=2.8 EndZ=0
    g3: ArcOfCircle CenterX=59.4 CenterY=2.4 CenterZ=0 NormalX=-1e-16 NormalY=0 NormalZ=1 AngleXU=3.90995e-07 Radius=1.5 StartAngle=0 EndAngle=1.5708
    g4: LineSegment StartX=60.9 StartY=-0.4 StartZ=0 EndX=60.9 EndY=2.4 EndZ=0
    g5: LineSegment StartX=76.4 StartY=-0.4 StartZ=0 EndX=60.9 EndY=-0.4 EndZ=0
    g6: ArcOfCircle CenterX=76.4 CenterY=-1.9 CenterZ=0 NormalX=-1e-16 NormalY=0 NormalZ=1 AngleXU=3.90995e-07 Radius=1.5 StartAngle=0 EndAngle=1.5708
    g7: LineSegment StartX=77.9 StartY=-6.3 StartZ=0 EndX=77.9 EndY=-1.9 EndZ=0
    g8: LineSegment StartX=96.4 StartY=-6.3 StartZ=0 EndX=77.9 EndY=-6.3 EndZ=0
    g9: ArcOfCircle CenterX=96.4 CenterY=-7.8 CenterZ=0 NormalX=-1e-16 NormalY=0 NormalZ=1 AngleXU=3.90995e-07 Radius=1.5 StartAngle=0 EndAngle=1.5708
    g10: LineSegment StartX=97.9 StartY=-59.8 StartZ=0 EndX=97.9 EndY=-7.8 EndZ=0
    g11: LineSegment StartX=97.9 StartY=-72.8 StartZ=0 EndX=97.9 EndY=-59.8 EndZ=0
    g12: ArcOfCircle CenterX=96.4 CenterY=-72.8 CenterZ=0 NormalX=-1e-16 NormalY=0 NormalZ=1 AngleXU=-1.5708 Radius=1.5 StartAngle=0 EndAngle=1.5708
    g13: LineSegment StartX=78 StartY=-74.3 StartZ=0 EndX=96.4 EndY=-74.3 EndZ=0
    g14: ArcOfCircle CenterX=78 CenterY=-72.8 CenterZ=0 NormalX=-1e-16 NormalY=0 NormalZ=1 AngleXU=-3.14159 Radius=1.5 StartAngle=0 EndAngle=1.5708
    g15: LineSegment StartX=76.5 StartY=-68.4 StartZ=0 EndX=76.5 EndY=-72.8 EndZ=0
    g16: LineSegment StartX=68.6 StartY=-68.4 StartZ=0 EndX=76.5 EndY=-68.4 EndZ=0
    g17: LineSegment StartX=68.6 StartY=-69.9 StartZ=0 EndX=68.6 EndY=-68.4 EndZ=0
    g18: LineSegment StartX=75 StartY=-69.9 StartZ=0 EndX=68.6 EndY=-69.9 EndZ=0
    g19: LineSegment StartX=75 StartY=-72.8 StartZ=0 EndX=75 EndY=-69.9 EndZ=0
    g20: ArcOfCircle CenterX=73.5 CenterY=-72.8 CenterZ=0 NormalX=-1e-16 NormalY=0 NormalZ=1 AngleXU=-1.5708 Radius=1.5 StartAngle=0 EndAngle=1.5708
    g21: LineSegment StartX=46.1 StartY=-74.3 StartZ=0 EndX=73.5 EndY=-74.3 EndZ=0
    g22: ArcOfCircle CenterX=46.1 CenterY=-72.8 CenterZ=0 NormalX=-1e-16 NormalY=0 NormalZ=1 AngleXU=-3.14159 Radius=1.5 StartAngle=0 EndAngle=1.5708
    g23: LineSegment StartX=44.6 StartY=-67.6 StartZ=0 EndX=44.6 EndY=-72.8 EndZ=0
    g24: LineSegment StartX=49.65 StartY=-67.6 StartZ=0 EndX=44.6 EndY=-67.6 EndZ=0
    g25: LineSegment StartX=49.65 StartY=-66.1 StartZ=0 EndX=49.65 EndY=-67.6 EndZ=0
    g26: LineSegment StartX=43.1 StartY=-66.1 StartZ=0 EndX=49.65 EndY=-66.1 EndZ=0
    g27: LineSegment StartX=43.1 StartY=-71.2 StartZ=0 EndX=43.1 EndY=-66.1 EndZ=0
    g28: ArcOfCircle CenterX=41.6 CenterY=-71.2 CenterZ=0 NormalX=-1e-16 NormalY=0 NormalZ=1 AngleXU=-1.5708 Radius=1.5 StartAngle=0 EndAngle=1.5708
    g29: LineSegment StartX=41.4 StartY=-72.7 StartZ=0 EndX=41.6 EndY=-72.7 EndZ=0
    g30: LineSegment StartX=24.227 StartY=-72.7043 StartZ=0 EndX=41.4 EndY=-72.7 EndZ=0
    g31: LineSegment StartX=6.18739 StartY=-75.9853 StartZ=0 EndX=24.227 EndY=-72.7043 EndZ=0
    g32: LineSegment StartX=-12.4977 StartY=-82.7894 StartZ=0 EndX=6.18739 EndY=-75.9853 EndZ=0
    g33: ArcOfCircle CenterX=-13.011 CenterY=-81.3799 CenterZ=0 NormalX=-1e-16 NormalY=0 NormalZ=1 AngleXU=-2.78726 Radius=1.5 StartAngle=0 EndAngle=1.56568
    g34: LineSegment StartX=-22.1 StartY=-61.1344 StartZ=0 EndX=-14.4178 EndY=-81.9004 EndZ=0
    g35: LineSegment StartX=-22.1 StartY=0 StartZ=0 EndX=-22.1 EndY=-61.1344 EndZ=0
    g36: LineSegment StartX=-16.4 StartY=0 StartZ=0 EndX=-22.1 EndY=0 EndZ=0
    g37: LineSegment StartX=-16.4 StartY=-10.5 StartZ=0 EndX=-16.4 EndY=0 EndZ=0
    g38: LineSegment StartX=-14.8 StartY=-10.5 StartZ=0 EndX=-16.4 EndY=-10.5 EndZ=0
    g39: LineSegment StartX=-14.8 StartY=0 StartZ=0 EndX=-14.8 EndY=-10.5 EndZ=0
    g40: LineSegment StartX=-5 StartY=0 StartZ=0 EndX=-14.8 EndY=0 EndZ=0
    g41: LineSegment StartX=-5 StartY=-4 StartZ=0 EndX=-5 EndY=0 EndZ=0
    g42: LineSegment StartX=5 StartY=-4 StartZ=0 EndX=-5 EndY=-4 EndZ=0
    g43: LineSegment StartX=5 StartY=0 StartZ=0 EndX=5 EndY=-4 EndZ=0
    g44: LineSegment StartX=9.9 StartY=0 StartZ=0 EndX=5 EndY=0 EndZ=0
    g45: LineSegment StartX=9.9 StartY=1.3 StartZ=0 EndX=9.9 EndY=0 EndZ=0
    g46: LineSegment StartX=23.7 StartY=1.3 StartZ=0 EndX=9.9 EndY=1.3 EndZ=0
    g47: ArcOfCircle CenterX=25.2 CenterY=1.3 CenterZ=0 NormalX=-1e-16 NormalY=0 NormalZ=1 AngleXU=1.5708 Radius=1.5 StartAngle=0 EndAngle=1.5708
    g48: LineSegment StartX=43.8874 StartY=2.8 StartZ=0 EndX=25.2 EndY=2.8 EndZ=0
    g49: Circle CenterX=95.6 CenterY=-57.3 CenterZ=0 NormalX=-1e-16 NormalY=0 NormalZ=1 AngleXU=-1.5708 Radius=1.1
    g50: ArcOfCircle CenterX=60.7 CenterY=-66.9 CenterZ=0 NormalX=-1e-16 NormalY=0 NormalZ=1 AngleXU=-3.14159 Radius=1.5 StartAngle=0 EndAngle=1.5708
    g51: LineSegment StartX=59.2 StartY=-66.1 StartZ=0 EndX=59.2 EndY=-66.9 EndZ=0
    g52: LineSegment StartX=51.15 StartY=-66.1 StartZ=0 EndX=59.2 EndY=-66.1 EndZ=0
    g53: LineSegment StartX=51.15 StartY=-67.6 StartZ=0 EndX=51.15 EndY=-66.1 EndZ=0
    g54: LineSegment StartX=56.7 StartY=-67.6 StartZ=0 EndX=51.15 EndY=-67.6 EndZ=0
    g55: LineSegment StartX=56.7 StartY=-69.9 StartZ=0 EndX=56.7 EndY=-67.6 EndZ=0
    g56: LineSegment StartX=67.1 StartY=-69.9 StartZ=0 EndX=56.7 EndY=-69.9 EndZ=0
    g57: LineSegment StartX=67.1 StartY=-68.4 StartZ=0 EndX=67.1 EndY=-69.9 EndZ=0
    g58: LineSegment StartX=60.7 StartY=-68.4 StartZ=0 EndX=67.1 EndY=-68.4 EndZ=0
    g59: LineSegment StartX=62.7 StartY=-60 StartZ=0 EndX=27.8 EndY=-60 EndZ=0
    g60: LineSegment StartX=62.7 StartY=-57.6 StartZ=0 EndX=62.7 EndY=-60 EndZ=0
    g61: LineSegment StartX=27.8 StartY=-57.6 StartZ=0 EndX=62.7 EndY=-57.6 EndZ=0
    g62: LineSegment StartX=27.8 StartY=-60 StartZ=0 EndX=27.8 EndY=-57.6 EndZ=0
    g63: Circle CenterX=-14 CenterY=-73.8 CenterZ=0 NormalX=-1e-16 NormalY=0 NormalZ=1 AngleXU=-1.5708 Radius=1.1
    g64: LineSegment StartX=-14.8 StartY=-64.1 StartZ=0 EndX=-16.4 EndY=-64.1 EndZ=0
    g65: LineSegment StartX=-14.8 StartY=-54 StartZ=0 EndX=-14.8 EndY=-64.1 EndZ=0
    g66: LineSegment StartX=-16.4 StartY=-54 StartZ=0 EndX=-14.8 EndY=-54 EndZ=0
    g67: LineSegment StartX=-16.4 StartY=-64.1 StartZ=0 EndX=-16.4 EndY=-54 EndZ=0
    g68: LineSegment StartX=52 StartY=-56.2 StartZ=0 EndX=27.8 EndY=-56.2 EndZ=0
    g69: LineSegment StartX=52 StartY=-53.8 StartZ=0 EndX=52 EndY=-56.2 EndZ=0
    g70: LineSegment StartX=27.8 StartY=-53.8 StartZ=0 EndX=52 EndY=-53.8 EndZ=0
    g71: LineSegment StartX=27.8 StartY=-56.2 StartZ=0 EndX=27.8 EndY=-53.8 EndZ=0
    g72: Circle CenterX=95.6 CenterY=-23.3 CenterZ=0 NormalX=-1e-16 NormalY=0 NormalZ=1 AngleXU=-1.5708 Radius=1.1
    g73: Circle CenterX=25.9 CenterY=0.6 CenterZ=0 NormalX=-1e-16 NormalY=0 NormalZ=1 AngleXU=-1.5708 Radius=1.1
  constraints (144):
    c: Coincident(g34,g35)
    c: Coincident(g35,g36)
    c: Coincident(g64,g67)
    c: Coincident(g66,g67)
    c: Coincident(g37,g38)
    c: Coincident(g36,g37)
    c: Coincident(g64,g65)
    c: Coincident(g65,g66)
    c: Coincident(g38,g39)
    c: Coincident(g39,g40)
    c: Coincident(g33,g34)
    c: Coincident(g32,g33)
    c: Coincident(g41,g42)
    c: Coincident(g40,g41)
    c: Coincident(g42,g43)
    c: Coincident(g43,g44)
    c: Coincident(g31,g32)
    c: Coincident(g44,g45)
    c: Coincident(g45,g46)
    c: Coincident(g46,g47)
    c: Coincident(g30,g31)
    c: Coincident(g47,g48)
    c: Coincident(g59,g62)
    c: Coincident(g61,g62)
    c: Coincident(g68,g71)
    c: Coincident(g70,g71)
    c: Coincident(g29,g30)
    c: Coincident(g28,g29)
    c: Coincident(g27,g28)
    c: Coincident(g26,g27)
    c: Coincident(g2,g48)
    c: Coincident(g0,g2)
    c: Coincident(g22,g23)
    c: Coincident(g23,g24)
    c: Coincident(g0,g1)
    c: Coincident(g21,g22)
    c: Coincident(g24,g25)
    c: Coincident(g25,g26)
    c: Coincident(g53,g54)
    c: Coincident(g52,g53)
    c: Coincident(g68,g69)
    c: Coincident(g69,g70)
    c: Coincident(g55,g56)
    c: Coincident(g54,g55)
    c: Coincident(g50,g51)
    c: Coincident(g51,g52)
    c: Coincident(g1,g3)
    c: Coincident(g50,g58)
    c: Coincident(g4,g5)
    c: Coincident(g3,g4)
    c: Coincident(g59,g60)
    c: Coincident(g60,g61)
    c: Coincident(g56,g57)
    c: Coincident(g57,g58)
    c: Coincident(g17,g18)
    c: Coincident(g16,g17)
    c: Coincident(g20,g21)
    c: Coincident(g19,g20)
    c: Coincident(g18,g19)
    c: Coincident(g5,g6)
    c: Coincident(g14,g15)
    c: Coincident(g15,g16)
    c: Coincident(g7,g8)
    c: Coincident(g6,g7)
    c: Coincident(g13,g14)
    c: Coincident(g12,g13)
    c: Coincident(g8,g9)
    c: Coincident(g11,g12)
    c: Coincident(g10,g11)
    c: Coincident(g9,g10)
    c: Block(g0)
    c: Block(g1)
    c: Block(g2)
    c: Block(g3)
    c: Block(g4)
    c: Block(g5)
    c: Block(g6)
    c: Block(g7)
    c: Block(g8)
    c: Block(g9)
    c: Block(g10)
    c: Block(g11)
    c: Block(g12)
    c: Block(g13)
    c: Block(g14)
    c: Block(g15)
    c: Block(g16)
    c: Block(g17)
    c: Block(g18)
    c: Block(g19)
    c: Block(g20)
    c: Block(g21)
    c: Block(g22)
    c: Block(g23)
    c: Block(g24)
    c: Block(g25)
    c: Block(g26)
    c: Block(g27)
    c: Block(g28)
    c: Block(g29)
    c: Block(g30)
    c: Block(g31)
    c: Block(g32)
    c: Block(g33)
    c: Block(g34)
    c: Block(g35)
    c: Block(g36)
    c: Block(g37)
    c: Block(g38)
    c: Block(g39)
    c: Block(g40)
    c: Block(g41)
    c: Block(g42)
    c: Block(g43)
    c: Block(g44)
    c: Block(g45)
    c: Block(g46)
    c: Block(g47)
    c: Block(g48)
    c: Block(g49)
    c: Block(g50)
    c: Block(g51)
    c: Block(g52)
    c: Block(g53)
    c: Block(g54)
    c: Block(g55)
    c: Block(g56)
    c: Block(g57)
    c: Block(g58)
    c: Block(g59)
    c: Block(g60)
    c: Block(g61)
    c: Block(g62)
    c: Block(g63)
    c: Block(g64)
    c: Block(g65)
    c: Block(g66)
    c: Block(g67)
    c: Block(g68)
    c: Block(g69)
    c: Block(g70)
    c: Block(g71)
    c: Block(g72)
    c: Block(g73)
FEATURE [Sketcher::SketchObject] Sketch023
  ArcFitTolerance = 1e-06
  AttachmentOffset = pos=(0,0,-5.1) rot=(0,0,1;0rad)
  AttachmentSupport = -> [XY_Plane004]
  FullyConstrained = false
  MakeInternals = false
  MapMode = 5
  Placement = pos=(0,0,-5.1) rot=(0,0,1;0rad)
  sketch-geometry (96):
    g0: ArcOfCircle [constr] CenterX=45.3 CenterY=2.4 CenterZ=0 NormalX=-1e-16 NormalY=0 NormalZ=1 AngleXU=1.5708 Radius=1.5 StartAngle=0 EndAngle=1.22777
    g1: LineSegment [constr] StartX=59.4 StartY=3.9 StartZ=0 EndX=45.3 EndY=3.9 EndZ=0
    g2: LineSegment [constr] StartX=43.8874 StartY=2.9045 StartZ=0 EndX=43.8874 EndY=2.8 EndZ=0
    g3: ArcOfCircle [constr] CenterX=59.4 CenterY=2.4 CenterZ=0 NormalX=-1e-16 NormalY=0 NormalZ=1 AngleXU=3.90995e-07 Radius=1.5 StartAngle=0 EndAngle=1.5708
    g4: LineSegment [constr] StartX=60.9 StartY=-0.4 StartZ=0 EndX=60.9 EndY=2.4 EndZ=0
    g5: LineSegment [constr] StartX=76.4 StartY=-0.4 StartZ=0 EndX=60.9 EndY=-0.4 EndZ=0
    g6: ArcOfCircle [constr] CenterX=76.4 CenterY=-1.9 CenterZ=0 NormalX=-1e-16 NormalY=0 NormalZ=1 AngleXU=3.90995e-07 Radius=1.5 StartAngle=0 EndAngle=1.5708
    g7: LineSegment [constr] StartX=77.9 StartY=-6.3 StartZ=0 EndX=77.9 EndY=-1.9 EndZ=0
    g8: LineSegment [constr] StartX=96.4 StartY=-6.3 StartZ=0 EndX=77.9 EndY=-6.3 EndZ=0
    g9: ArcOfCircle [constr] CenterX=96.4 CenterY=-7.8 CenterZ=0 NormalX=-1e-16 NormalY=0 NormalZ=1 AngleXU=3.90995e-07 Radius=1.5 StartAngle=0 EndAngle=1.5708
    g10: LineSegment [constr] StartX=97.9 StartY=-59.8 StartZ=0 EndX=97.9 EndY=-7.8 EndZ=0
    g11: LineSegment [constr] StartX=97.9 StartY=-72.8 StartZ=0 EndX=97.9 EndY=-59.8 EndZ=0
    g12: ArcOfCircle [constr] CenterX=96.4 CenterY=-72.8 CenterZ=0 NormalX=-1e-16 NormalY=0 NormalZ=1 AngleXU=-1.5708 Radius=1.5 StartAngle=0 EndAngle=1.5708
    g13: LineSegment [constr] StartX=78 StartY=-74.3 StartZ=0 EndX=96.4 EndY=-74.3 EndZ=0
    g14: ArcOfCircle [constr] CenterX=78 CenterY=-72.8 CenterZ=0 NormalX=-1e-16 NormalY=0 NormalZ=1 AngleXU=-3.14159 Radius=1.5 StartAngle=0 EndAngle=1.5708
    g15: LineSegment [constr] StartX=76.5 StartY=-68.4 StartZ=0 EndX=76.5 EndY=-72.8 EndZ=0
    g16: LineSegment [constr] StartX=68.6 StartY=-68.4 StartZ=0 EndX=76.5 EndY=-68.4 EndZ=0
    g17: LineSegment [constr] StartX=43.1 StartY=-66.1 StartZ=0 EndX=49.65 EndY=-66.1 EndZ=0
    g18: LineSegment [constr] StartX=43.1 StartY=-71.2 StartZ=0 EndX=43.1 EndY=-66.1 EndZ=0
    g19: ArcOfCircle [constr] CenterX=41.6 CenterY=-71.2 CenterZ=0 NormalX=-1e-16 NormalY=0 NormalZ=1 AngleXU=-1.5708 Radius=1.5 StartAngle=0 EndAngle=1.5708
    g20: LineSegment [constr] StartX=41.4 StartY=-72.7 StartZ=0 EndX=41.6 EndY=-72.7 EndZ=0
    g21: LineSegment [constr] StartX=24.227 StartY=-72.7043 StartZ=0 EndX=41.4 EndY=-72.7 EndZ=0
    g22: LineSegment [constr] StartX=6.18739 StartY=-75.9853 StartZ=0 EndX=24.227 EndY=-72.7043 EndZ=0
    g23: LineSegment [constr] StartX=-12.4977 StartY=-82.7894 StartZ=0 EndX=6.18739 EndY=-75.9853 EndZ=0
    g24: ArcOfCircle [constr] CenterX=-13.011 CenterY=-81.3799 CenterZ=0 NormalX=-1e-16 NormalY=0 NormalZ=1 AngleXU=-2.78726 Radius=1.5 StartAngle=0 EndAngle=1.56568
    g25: LineSegment [constr] StartX=-22.1 StartY=-61.1344 StartZ=0 EndX=-14.4178 EndY=-81.9004 EndZ=0
    g26: LineSegment [constr] StartX=-22.1 StartY=0 StartZ=0 EndX=-22.1 EndY=-61.1344 EndZ=0
    g27: LineSegment [constr] StartX=9.9 StartY=0 StartZ=0 EndX=5 EndY=0 EndZ=0
    g28: LineSegment [constr] StartX=9.9 StartY=1.3 StartZ=0 EndX=9.9 EndY=0 EndZ=0
    g29: LineSegment [constr] StartX=23.7 StartY=1.3 StartZ=0 EndX=9.9 EndY=1.3 EndZ=0
    g30: ArcOfCircle [constr] CenterX=25.2 CenterY=1.3 CenterZ=0 NormalX=-1e-16 NormalY=0 NormalZ=1 AngleXU=1.5708 Radius=1.5 StartAngle=0 EndAngle=1.5708
    g31: LineSegment [constr] StartX=43.8874 StartY=2.8 StartZ=0 EndX=25.2 EndY=2.8 EndZ=0
    g32: Circle [constr] CenterX=95.6 CenterY=-57.3 CenterZ=0 NormalX=-1e-16 NormalY=0 NormalZ=1 AngleXU=-1.5708 Radius=1.1
    g33: ArcOfCircle [constr] CenterX=60.7 CenterY=-66.9 CenterZ=0 NormalX=-1e-16 NormalY=0 NormalZ=1 AngleXU=-3.14159 Radius=1.5 StartAngle=0 EndAngle=1.5708
    g34: LineSegment [constr] StartX=59.2 StartY=-66.1 StartZ=0 EndX=59.2 EndY=-66.9 EndZ=0
    g35: LineSegment [constr] StartX=51.15 StartY=-66.1 StartZ=0 EndX=59.2 EndY=-66.1 EndZ=0
    g36: LineSegment [constr] StartX=60.7 StartY=-68.4 StartZ=0 EndX=67.1 EndY=-68.4 EndZ=0
    g37: LineSegment [constr] StartX=62.7 StartY=-60 StartZ=0 EndX=27.8 EndY=-60 EndZ=0
    g38: LineSegment [constr] StartX=62.7 StartY=-57.6 StartZ=0 EndX=62.7 EndY=-60 EndZ=0
    g39: LineSegment [constr] StartX=27.8 StartY=-57.6 StartZ=0 EndX=62.7 EndY=-57.6 EndZ=0
    g40: LineSegment [constr] StartX=27.8 StartY=-60 StartZ=0 EndX=27.8 EndY=-57.6 EndZ=0
    g41: Circle [constr] CenterX=-14 CenterY=-73.8 CenterZ=0 NormalX=-1e-16 NormalY=0 NormalZ=1 AngleXU=-1.5708 Radius=1.1
    g42: LineSegment [constr] StartX=-14.8 StartY=-64.1 StartZ=0 EndX=-16.4 EndY=-64.1 EndZ=0
    g43: LineSegment [constr] StartX=-14.8 StartY=-54 StartZ=0 EndX=-14.8 EndY=-64.1 EndZ=0
    g44: LineSegment [constr] StartX=-16.4 StartY=-54 StartZ=0 EndX=-14.8 EndY=-54 EndZ=0
    g45: LineSegment [constr] StartX=-16.4 StartY=-64.1 StartZ=0 EndX=-16.4 EndY=-54 EndZ=0
    g46: LineSegment [constr] StartX=52 StartY=-56.2 StartZ=0 EndX=27.8 EndY=-56.2 EndZ=0
    g47: LineSegment [constr] StartX=52 StartY=-53.8 StartZ=0 EndX=52 EndY=-56.2 EndZ=0
    g48: LineSegment [constr] StartX=27.8 StartY=-53.8 StartZ=0 EndX=52 EndY=-53.8 EndZ=0
    g49: LineSegment [constr] StartX=27.8 StartY=-56.2 StartZ=0 EndX=27.8 EndY=-53.8 EndZ=0
    g50: Circle [constr] CenterX=95.6 CenterY=-23.3 CenterZ=0 NormalX=-1e-16 NormalY=0 NormalZ=1 AngleXU=-1.5708 Radius=1.1
    g51: Circle [constr] CenterX=25.9 CenterY=0.6 CenterZ=0 NormalX=-1e-16 NormalY=0 NormalZ=1 AngleXU=-1.5708 Radius=1.1
    g52: LineSegment [constr] StartX=49.65 StartY=-66.1 StartZ=0 EndX=51.15 EndY=-66.1 EndZ=0
    g53: LineSegment [constr] StartX=67.1 StartY=-68.4 StartZ=0 EndX=68.6 EndY=-68.4 EndZ=0
    g54: LineSegment [constr] StartX=-22.1 StartY=0 StartZ=0 EndX=5 EndY=0 EndZ=0
    g55: LineSegment StartX=-22.1 StartY=0.3 StartZ=0 EndX=5 EndY=0.3 EndZ=0
    g56: LineSegment StartX=9.6 StartY=0.3 StartZ=0 EndX=5 EndY=0.3 EndZ=0
    g57: LineSegment StartX=9.6 StartY=1.3 StartZ=0 EndX=9.6 EndY=0.3 EndZ=0
    g58: ArcOfCircle CenterX=9.9 CenterY=1.3 CenterZ=0 NormalX=0 NormalY=0 NormalZ=1 AngleXU=0 Radius=0.3 StartAngle=1.5708 EndAngle=3.14159
    g59: LineSegment StartX=23.4252 StartY=1.6 StartZ=0 EndX=9.9 EndY=1.6 EndZ=0
    g60: ArcOfCircle CenterX=25.2 CenterY=1.3 CenterZ=0 NormalX=0 NormalY=0 NormalZ=1 AngleXU=1.5708 Radius=1.8 StartAngle=0 EndAngle=1.40335
    g61: LineSegment StartX=43.6417 StartY=3.1 StartZ=0 EndX=25.2 EndY=3.1 EndZ=0
    g62: ArcOfCircle CenterX=45.3 CenterY=2.4 CenterZ=0 NormalX=0 NormalY=0 NormalZ=1 AngleXU=1.5708 Radius=1.8 StartAngle=0 EndAngle=1.17137
    g63: LineSegment StartX=59.4 StartY=4.2 StartZ=0 EndX=45.3 EndY=4.2 EndZ=0
    g64: ArcOfCircle CenterX=59.4 CenterY=2.4 CenterZ=0 NormalX=0 NormalY=0 NormalZ=1 AngleXU=3.90995e-07 Radius=1.8 StartAngle=-1.8e-15 EndAngle=1.5708
    g65: LineSegment StartX=61.2 StartY=-0.1 StartZ=0 EndX=61.2 EndY=2.4 EndZ=0
    g66: LineSegment StartX=76.4 StartY=-0.1 StartZ=0 EndX=61.2 EndY=-0.1 EndZ=0
    g67: ArcOfCircle CenterX=76.4 CenterY=-1.9 CenterZ=0 NormalX=0 NormalY=0 NormalZ=1 AngleXU=3.90995e-07 Radius=1.8 StartAngle=-1.8e-15 EndAngle=1.5708
    g68: LineSegment StartX=78.2 StartY=-6 StartZ=0 EndX=78.2 EndY=-1.9 EndZ=0
    g69: LineSegment StartX=96.4 StartY=-6 StartZ=0 EndX=78.2 EndY=-6 EndZ=0
    g70: ArcOfCircle CenterX=96.4 CenterY=-7.8 CenterZ=0 NormalX=0 NormalY=0 NormalZ=1 AngleXU=3.90995e-07 Radius=1.8 StartAngle=9e-16 EndAngle=1.5708
    g71: LineSegment StartX=98.2 StartY=-59.8 StartZ=0 EndX=98.2 EndY=-7.8 EndZ=0
    g72: LineSegment StartX=98.2 StartY=-72.8 StartZ=0 EndX=98.2 EndY=-59.8 EndZ=0
    g73: ArcOfCircle CenterX=96.4 CenterY=-72.8 CenterZ=0 NormalX=0 NormalY=0 NormalZ=1 AngleXU=-1.5708 Radius=1.8 StartAngle=0 EndAngle=1.5708
    g74: LineSegment StartX=78 StartY=-74.6 StartZ=0 EndX=96.4 EndY=-74.6 EndZ=0
    g75: ArcOfCircle CenterX=78 CenterY=-72.8 CenterZ=0 NormalX=0 NormalY=0 NormalZ=1 AngleXU=-3.14159 Radius=1.8 StartAngle=0 EndAngle=1.5708
    g76: LineSegment StartX=76.2 StartY=-68.7 StartZ=0 EndX=76.2 EndY=-72.8 EndZ=0
    g77: LineSegment StartX=68.6 StartY=-68.7 StartZ=0 EndX=76.2 EndY=-68.7 EndZ=0
    g78: LineSegment StartX=67.1 StartY=-68.7 StartZ=0 EndX=68.6 EndY=-68.7 EndZ=0
    g79: LineSegment StartX=60.7 StartY=-68.7 StartZ=0 EndX=67.1 EndY=-68.7 EndZ=0
    g80: ArcOfCircle CenterX=60.7 CenterY=-66.9 CenterZ=0 NormalX=0 NormalY=0 NormalZ=1 AngleXU=-3.14159 Radius=1.8 StartAngle=0 EndAngle=1.5708
    g81: LineSegment StartX=58.9 StartY=-66.4 StartZ=0 EndX=58.9 EndY=-66.9 EndZ=0
    g82: LineSegment StartX=51.15 StartY=-66.4 StartZ=0 EndX=58.9 EndY=-66.4 EndZ=0
    g83: LineSegment StartX=49.65 StartY=-66.4 StartZ=0 EndX=51.15 EndY=-66.4 EndZ=0
    g84: LineSegment StartX=43.4 StartY=-66.4 StartZ=0 EndX=49.65 EndY=-66.4 EndZ=0
    g85: LineSegment StartX=43.4 StartY=-71.2 StartZ=0 EndX=43.4 EndY=-66.4 EndZ=0
    g86: ArcOfCircle CenterX=41.6 CenterY=-71.2 CenterZ=0 NormalX=0 NormalY=0 NormalZ=1 AngleXU=-1.5708 Radius=1.8 StartAngle=0 EndAngle=1.5708
    g87: LineSegment StartX=41.4 StartY=-73 StartZ=0 EndX=41.6 EndY=-73 EndZ=0
    g88: LineSegment StartX=24.2541 StartY=-73.0043 StartZ=0 EndX=41.4 EndY=-73 EndZ=0
    g89: LineSegment StartX=6.26611 StartY=-76.2759 StartZ=0 EndX=24.2541 EndY=-73.0043 EndZ=0
    g90: LineSegment StartX=-12.3951 StartY=-83.0713 StartZ=0 EndX=6.26611 EndY=-76.2759 EndZ=0
    g91: ArcOfCircle CenterX=-13.011 CenterY=-81.3799 CenterZ=0 NormalX=0 NormalY=0 NormalZ=1 AngleXU=-2.78726 Radius=1.8 StartAngle=6.28319 EndAngle=7.84887
    g92: LineSegment StartX=-22.3814 StartY=-61.2385 StartZ=0 EndX=-14.6992 EndY=-82.0044 EndZ=0
    g93: ArcOfCircle CenterX=-22.1 CenterY=-61.1344 CenterZ=0 NormalX=0 NormalY=0 NormalZ=1 AngleXU=1.5708 Radius=0.3 StartAngle=1.5708 EndAngle=1.92513
    g94: LineSegment StartX=-22.4 StartY=0 StartZ=0 EndX=-22.4 EndY=-61.1344 EndZ=0
    g95: ArcOfCircle CenterX=-22.1 CenterY=0 CenterZ=0 NormalX=0 NormalY=0 NormalZ=1 AngleXU=0 Radius=0.3 StartAngle=1.5708 EndAngle=3.14159
  constraints (147):
    c: Coincident(g25,g26)
    c: Coincident(g42,g45)
    c: Coincident(g44,g45)
    c: Coincident(g42,g43)
    c: Coincident(g43,g44)
    c: Coincident(g24,g25)
    c: Coincident(g23,g24)
    c: Coincident(g22,g23)
    c: Coincident(g27,g28)
    c: Coincident(g28,g29)
    c: Coincident(g29,g30)
    c: Coincident(g21,g22)
    c: Coincident(g30,g31)
    c: Coincident(g37,g40)
    c: Coincident(g39,g40)
    c: Coincident(g46,g49)
    c: Coincident(g48,g49)
    c: Coincident(g20,g21)
    c: Coincident(g19,g20)
    c: Coincident(g18,g19)
    c: Coincident(g17,g18)
    c: Coincident(g2,g31)
    c: Coincident(g0,g2)
    c: Coincident(g0,g1)
    c: Coincident(g46,g47)
    c: Coincident(g47,g48)
    c: Coincident(g33,g34)
    c: Coincident(g34,g35)
    c: Coincident(g1,g3)
    c: Coincident(g33,g36)
    c: Coincident(g4,g5)
    c: Coincident(g3,g4)
    c: Coincident(g37,g38)
    c: Coincident(g38,g39)
    c: Coincident(g5,g6)
    c: Coincident(g14,g15)
    c: Coincident(g15,g16)
    c: Coincident(g7,g8)
    c: Coincident(g6,g7)
    c: Coincident(g13,g14)
    c: Coincident(g12,g13)
    c: Coincident(g8,g9)
    c: Coincident(g11,g12)
    c: Coincident(g10,g11)
    c: Coincident(g9,g10)
    c: Block(g0)
    c: Block(g1)
    c: Block(g2)
    c: Block(g3)
    c: Block(g4)
    c: Block(g5)
    c: Block(g6)
    c: Block(g7)
    c: Block(g8)
    c: Block(g9)
    c: Block(g10)
    c: Block(g11)
    c: Block(g12)
    c: Block(g13)
    c: Block(g14)
    c: Block(g15)
    c: Block(g16)
    c: Block(g17)
    c: Block(g18)
    c: Block(g19)
    c: Block(g20)
    c: Block(g21)
    c: Block(g22)
    c: Block(g23)
    c: Block(g24)
    c: Block(g25)
    c: Block(g26)
    c: Block(g27)
    c: Block(g28)
    c: Block(g29)
    c: Block(g30)
    c: Block(g31)
    c: Block(g32)
    c: Block(g33)
    c: Block(g34)
    c: Block(g35)
    c: Block(g36)
    c: Block(g37)
    c: Block(g38)
    c: Block(g39)
    c: Block(g40)
    c: Block(g41)
    c: Block(g42)
    c: Block(g43)
    c: Block(g44)
    c: Block(g45)
    c: Block(g46)
    c: Block(g47)
    c: Block(g48)
    c: Block(g49)
    c: Block(g50)
    c: Block(g51)
    c: Coincident(g52,g17)
    c: Coincident(g52,g35)
    c: Horizontal(g52)
    c: Coincident(g53,g36)
    c: Coincident(g53,g16)
    c: Horizontal(g53)
    c: Coincident(g54,g26)
    c: Coincident(g54,g27)
    c: Horizontal(g54)
    c: Coincident(g55,g56)
    c: Tangent(g55,g95) = 1.5708
    c: Coincident(g56,g57)
    c: Tangent(g57,g58) = -1.5708
    c: Tangent(g58,g59) = -1.5708
    c: Coincident(g59,g60)
    c: Coincident(g61,g62)
    c: Coincident(g62,g63)
    c: Coincident(g65,g66)
    c: Coincident(g68,g69)
    c: Coincident(g71,g72)
    c: Coincident(g76,g77)
    c: Coincident(g77,g78)
    c: Coincident(g78,g79)
    c: Coincident(g81,g82)
    c: Coincident(g82,g83)
    c: Coincident(g83,g84)
    c: Coincident(g84,g85)
    c: Coincident(g87,g88)
    c: Coincident(g88,g89)
    c: Coincident(g89,g90)
    c: Tangent(g92,g93) = -1.5708
    c: Tangent(g93,g94) = -1.5708
    c: Tangent(g94,g95) = -1.5708
    c: Coincident(g91,g92)
    c: Coincident(g90,g91)
    c: Coincident(g60,g61)
    c: Coincident(g86,g87)
    c: Coincident(g85,g86)
    c: Coincident(g80,g81)
    c: Coincident(g63,g64)
    c: Coincident(g79,g80)
    c: Coincident(g64,g65)
    c: Coincident(g75,g76)
    c: Coincident(g66,g67)
    c: Coincident(g74,g75)
    c: Coincident(g67,g68)
    c: Coincident(g73,g74)
    c: Coincident(g69,g70)
    c: Coincident(g72,g73)
    c: Coincident(g70,g71)
FEATURE [PartDesign::Pocket] Pocket008
  BaseFeature = -> Pad010
  Direction = (0,0,-1)
  Length = 10
  Length2 = 5
  Profile = -> Sketch023
  ReferenceAxis = -> Sketch023 [N_Axis]
  Refine = true
  Reversed = true
  Suppressed = false
  Type = 0
FEATURE [Sketcher::SketchObject] Sketch024
  ArcFitTolerance = 1e-06
  AttachmentOffset = pos=(0,0,-5.1) rot=(0,0,1;0rad)
  AttachmentSupport = -> [XY_Plane004]
  FullyConstrained = false
  MakeInternals = false
  MapMode = 5
  Placement = pos=(0,0,-5.1) rot=(0,0,1;0rad)
  sketch-geometry (4):
    g0: LineSegment StartX=9.9 StartY=0 StartZ=0 EndX=9.9 EndY=7.12941 EndZ=0
    g1: LineSegment StartX=9.9 StartY=7.12941 StartZ=0 EndX=2.38364 EndY=7.12941 EndZ=0
    g2: LineSegment StartX=2.38364 StartY=7.12941 StartZ=0 EndX=2.38364 EndY=0 EndZ=0
    g3: LineSegment StartX=2.38364 StartY=0 StartZ=0 EndX=9.9 EndY=0 EndZ=0
  constraints (10):
    c: Coincident(g0,g1)
    c: Coincident(g1,g2)
    c: Coincident(g2,g3)
    c: Coincident(g3,g0)
    c: Vertical(g0)
    c: Vertical(g2)
    c: Horizontal(g1)
    c: Horizontal(g3)
    c: DistanceX(g-1,g0) = 9.9
    c: PointOnObject(g2,g-1)
FEATURE [PartDesign::Pocket] Pocket009
  BaseFeature = -> Pocket008
  Direction = (0,0,-1)
  Length = 10
  Length2 = 10
  Profile = -> Sketch024
  ReferenceAxis = -> Sketch024 [N_Axis]
  Refine = true
  Reversed = true
  Suppressed = false
  Type = 4
FEATURE [Sketcher::SketchObject] Sketch025
  ArcFitTolerance = 1e-06
  AttachmentSupport = -> [XY_Plane004]
  FullyConstrained = false
  MakeInternals = false
  MapMode = 5
  sketch-geometry (79):
    g0: ArcOfCircle [constr] CenterX=45.3 CenterY=2.4 CenterZ=0 NormalX=-1e-16 NormalY=0 NormalZ=1 AngleXU=1.5708 Radius=1.5 StartAngle=0 EndAngle=1.22777
    g1: LineSegment [constr] StartX=59.4 StartY=3.9 StartZ=0 EndX=45.3 EndY=3.9 EndZ=0
    g2: LineSegment [constr] StartX=43.8874 StartY=2.9045 StartZ=0 EndX=43.8874 EndY=2.8 EndZ=0
    g3: ArcOfCircle [constr] CenterX=59.4 CenterY=2.4 CenterZ=0 NormalX=-1e-16 NormalY=0 NormalZ=1 AngleXU=3.90995e-07 Radius=1.5 StartAngle=0 EndAngle=1.5708
    g4: LineSegment [constr] StartX=60.9 StartY=-0.4 StartZ=0 EndX=60.9 EndY=2.4 EndZ=0
    g5: LineSegment [constr] StartX=76.4 StartY=-0.4 StartZ=0 EndX=60.9 EndY=-0.4 EndZ=0
    g6: ArcOfCircle [constr] CenterX=76.4 CenterY=-1.9 CenterZ=0 NormalX=-1e-16 NormalY=0 NormalZ=1 AngleXU=3.90995e-07 Radius=1.5 StartAngle=0 EndAngle=1.5708
    g7: LineSegment [constr] StartX=77.9 StartY=-6.3 StartZ=0 EndX=77.9 EndY=-1.9 EndZ=0
    g8: LineSegment [constr] StartX=96.4 StartY=-6.3 StartZ=0 EndX=77.9 EndY=-6.3 EndZ=0
    g9: ArcOfCircle [constr] CenterX=96.4 CenterY=-7.8 CenterZ=0 NormalX=-1e-16 NormalY=0 NormalZ=1 AngleXU=3.90995e-07 Radius=1.5 StartAngle=0 EndAngle=1.5708
    g10: LineSegment [constr] StartX=97.9 StartY=-59.8 StartZ=0 EndX=97.9 EndY=-7.8 EndZ=0
    g11: LineSegment [constr] StartX=97.9 StartY=-72.8 StartZ=0 EndX=97.9 EndY=-59.8 EndZ=0
    g12: ArcOfCircle [constr] CenterX=96.4 CenterY=-72.8 CenterZ=0 NormalX=-1e-16 NormalY=0 NormalZ=1 AngleXU=-1.5708 Radius=1.5 StartAngle=0 EndAngle=1.5708
    g13: LineSegment [constr] StartX=78 StartY=-74.3 StartZ=0 EndX=96.4 EndY=-74.3 EndZ=0
    g14: ArcOfCircle [constr] CenterX=78 CenterY=-72.8 CenterZ=0 NormalX=-1e-16 NormalY=0 NormalZ=1 AngleXU=-3.14159 Radius=1.5 StartAngle=0 EndAngle=1.5708
    g15: LineSegment [constr] StartX=76.5 StartY=-68.4 StartZ=0 EndX=76.5 EndY=-72.8 EndZ=0
    g16: LineSegment [constr] StartX=68.6 StartY=-68.4 StartZ=0 EndX=76.5 EndY=-68.4 EndZ=0
    g17: LineSegment [constr] StartX=68.6 StartY=-69.9 StartZ=0 EndX=68.6 EndY=-68.4 EndZ=0
    g18: LineSegment [constr] StartX=75 StartY=-69.9 StartZ=0 EndX=68.6 EndY=-69.9 EndZ=0
    g19: LineSegment [constr] StartX=75 StartY=-72.8 StartZ=0 EndX=75 EndY=-69.9 EndZ=0
    g20: ArcOfCircle [constr] CenterX=73.5 CenterY=-72.8 CenterZ=0 NormalX=-1e-16 NormalY=0 NormalZ=1 AngleXU=-1.5708 Radius=1.5 StartAngle=0 EndAngle=1.5708
    g21: LineSegment [constr] StartX=46.1 StartY=-74.3 StartZ=0 EndX=73.5 EndY=-74.3 EndZ=0
    g22: ArcOfCircle [constr] CenterX=46.1 CenterY=-72.8 CenterZ=0 NormalX=-1e-16 NormalY=0 NormalZ=1 AngleXU=-3.14159 Radius=1.5 StartAngle=0 EndAngle=1.5708
    g23: LineSegment [constr] StartX=44.6 StartY=-67.6 StartZ=0 EndX=44.6 EndY=-72.8 EndZ=0
    g24: LineSegment [constr] StartX=49.65 StartY=-67.6 StartZ=0 EndX=44.6 EndY=-67.6 EndZ=0
    g25: LineSegment [constr] StartX=49.65 StartY=-66.1 StartZ=0 EndX=49.65 EndY=-67.6 EndZ=0
    g26: LineSegment [constr] StartX=43.1 StartY=-66.1 StartZ=0 EndX=49.65 EndY=-66.1 EndZ=0
    g27: LineSegment [constr] StartX=43.1 StartY=-71.2 StartZ=0 EndX=43.1 EndY=-66.1 EndZ=0
    g28: ArcOfCircle [constr] CenterX=41.6 CenterY=-71.2 CenterZ=0 NormalX=-1e-16 NormalY=0 NormalZ=1 AngleXU=-1.5708 Radius=1.5 StartAngle=0 EndAngle=1.5708
    g29: LineSegment [constr] StartX=41.4 StartY=-72.7 StartZ=0 EndX=41.6 EndY=-72.7 EndZ=0
    g30: LineSegment [constr] StartX=24.227 StartY=-72.7043 StartZ=0 EndX=41.4 EndY=-72.7 EndZ=0
    g31: LineSegment [constr] StartX=6.18739 StartY=-75.9853 StartZ=0 EndX=24.227 EndY=-72.7043 EndZ=0
    g32: LineSegment [constr] StartX=-12.4977 StartY=-82.7894 StartZ=0 EndX=6.18739 EndY=-75.9853 EndZ=0
    g33: ArcOfCircle [constr] CenterX=-13.011 CenterY=-81.3799 CenterZ=0 NormalX=-1e-16 NormalY=0 NormalZ=1 AngleXU=-2.78726 Radius=1.5 StartAngle=0 EndAngle=1.56568
    g34: LineSegment [constr] StartX=-22.1 StartY=-61.1344 StartZ=0 EndX=-14.4178 EndY=-81.9004 EndZ=0
    g35: LineSegment [constr] StartX=-22.1 StartY=0 StartZ=0 EndX=-22.1 EndY=-61.1344 EndZ=0
    g36: LineSegment [constr] StartX=-16.4 StartY=0 StartZ=0 EndX=-22.1 EndY=0 EndZ=0
    g37: LineSegment [constr] StartX=-16.4 StartY=-10.5 StartZ=0 EndX=-16.4 EndY=0 EndZ=0
    g38: LineSegment [constr] StartX=-14.8 StartY=-10.5 StartZ=0 EndX=-16.4 EndY=-10.5 EndZ=0
    g39: LineSegment [constr] StartX=-14.8 StartY=0 StartZ=0 EndX=-14.8 EndY=-10.5 EndZ=0
    g40: LineSegment [constr] StartX=-5 StartY=0 StartZ=0 EndX=-14.8 EndY=0 EndZ=0
    g41: LineSegment [constr] StartX=-5 StartY=-4 StartZ=0 EndX=-5 EndY=0 EndZ=0
    g42: LineSegment [constr] StartX=5 StartY=-4 StartZ=0 EndX=-5 EndY=-4 EndZ=0
    g43: LineSegment [constr] StartX=5 StartY=0 StartZ=0 EndX=5 EndY=-4 EndZ=0
    g44: LineSegment [constr] StartX=9.9 StartY=0 StartZ=0 EndX=5 EndY=0 EndZ=0
    g45: LineSegment [constr] StartX=9.9 StartY=1.3 StartZ=0 EndX=9.9 EndY=0 EndZ=0
    g46: LineSegment [constr] StartX=23.7 StartY=1.3 StartZ=0 EndX=9.9 EndY=1.3 EndZ=0
    g47: ArcOfCircle [constr] CenterX=25.2 CenterY=1.3 CenterZ=0 NormalX=-1e-16 NormalY=0 NormalZ=1 AngleXU=1.5708 Radius=1.5 StartAngle=0 EndAngle=1.5708
    g48: LineSegment [constr] StartX=43.8874 StartY=2.8 StartZ=0 EndX=25.2 EndY=2.8 EndZ=0
    g49: Circle [constr] CenterX=95.6 CenterY=-57.3 CenterZ=0 NormalX=-1e-16 NormalY=0 NormalZ=1 AngleXU=-1.5708 Radius=1.1
    g50: ArcOfCircle [constr] CenterX=60.7 CenterY=-66.9 CenterZ=0 NormalX=-1e-16 NormalY=0 NormalZ=1 AngleXU=-3.14159 Radius=1.5 StartAngle=0 EndAngle=1.5708
    g51: LineSegment [constr] StartX=59.2 StartY=-66.1 StartZ=0 EndX=59.2 EndY=-66.9 EndZ=0
    g52: LineSegment [constr] StartX=51.15 StartY=-66.1 StartZ=0 EndX=59.2 EndY=-66.1 EndZ=0
    g53: LineSegment [constr] StartX=51.15 StartY=-67.6 StartZ=0 EndX=51.15 EndY=-66.1 EndZ=0
    g54: LineSegment [constr] StartX=56.7 StartY=-67.6 StartZ=0 EndX=51.15 EndY=-67.6 EndZ=0
    g55: LineSegment [constr] StartX=56.7 StartY=-69.9 StartZ=0 EndX=56.7 EndY=-67.6 EndZ=0
    g56: LineSegment [constr] StartX=67.1 StartY=-69.9 StartZ=0 EndX=56.7 EndY=-69.9 EndZ=0
    g57: LineSegment [constr] StartX=67.1 StartY=-68.4 StartZ=0 EndX=67.1 EndY=-69.9 EndZ=0
    g58: LineSegment [constr] StartX=60.7 StartY=-68.4 StartZ=0 EndX=67.1 EndY=-68.4 EndZ=0
    g59: LineSegment [constr] StartX=62.7 StartY=-60 StartZ=0 EndX=27.8 EndY=-60 EndZ=0
    g60: LineSegment [constr] StartX=62.7 StartY=-57.6 StartZ=0 EndX=62.7 EndY=-60 EndZ=0
    g61: LineSegment [constr] StartX=27.8 StartY=-57.6 StartZ=0 EndX=62.7 EndY=-57.6 EndZ=0
    g62: LineSegment [constr] StartX=27.8 StartY=-60 StartZ=0 EndX=27.8 EndY=-57.6 EndZ=0
    g63: Circle [constr] CenterX=-14 CenterY=-73.8 CenterZ=0 NormalX=-1e-16 NormalY=0 NormalZ=1 AngleXU=-1.5708 Radius=1.1
    g64: LineSegment [constr] StartX=-14.8 StartY=-64.1 StartZ=0 EndX=-16.4 EndY=-64.1 EndZ=0
    g65: LineSegment [constr] StartX=-14.8 StartY=-54 StartZ=0 EndX=-14.8 EndY=-64.1 EndZ=0
    g66: LineSegment [constr] StartX=-16.4 StartY=-54 StartZ=0 EndX=-14.8 EndY=-54 EndZ=0
    g67: LineSegment [constr] StartX=-16.4 StartY=-64.1 StartZ=0 EndX=-16.4 EndY=-54 EndZ=0
    g68: LineSegment [constr] StartX=52 StartY=-56.2 StartZ=0 EndX=27.8 EndY=-56.2 EndZ=0
    g69: LineSegment [constr] StartX=52 StartY=-53.8 StartZ=0 EndX=52 EndY=-56.2 EndZ=0
    g70: LineSegment [constr] StartX=27.8 StartY=-53.8 StartZ=0 EndX=52 EndY=-53.8 EndZ=0
    g71: LineSegment [constr] StartX=27.8 StartY=-56.2 StartZ=0 EndX=27.8 EndY=-53.8 EndZ=0
    g72: Circle [constr] CenterX=95.6 CenterY=-23.3 CenterZ=0 NormalX=-1e-16 NormalY=0 NormalZ=1 AngleXU=-1.5708 Radius=1.1
    g73: Circle [constr] CenterX=25.9 CenterY=0.6 CenterZ=0 NormalX=-1e-16 NormalY=0 NormalZ=1 AngleXU=-1.5708 Radius=1.1
    g74: Circle CenterX=25.9 CenterY=0.6 CenterZ=0 NormalX=0 NormalY=0 NormalZ=1 AngleXU=0 Radius=1.2
    g75: Circle CenterX=25.9 CenterY=0.6 CenterZ=0 NormalX=0 NormalY=0 NormalZ=1 AngleXU=0 Radius=1.2
    g76: Circle CenterX=95.6 CenterY=-23.3 CenterZ=0 NormalX=0 NormalY=0 NormalZ=1 AngleXU=0 Radius=1.1
    g77: Circle CenterX=95.6 CenterY=-57.3 CenterZ=0 NormalX=0 NormalY=0 NormalZ=1 AngleXU=0 Radius=1.1
    g78: Circle CenterX=-14 CenterY=-73.8 CenterZ=0 NormalX=0 NormalY=0 NormalZ=1 AngleXU=0 Radius=1.2
  constraints (153):
    c: Coincident(g34,g35)
    c: Coincident(g35,g36)
    c: Coincident(g64,g67)
    c: Coincident(g66,g67)
    c: Coincident(g37,g38)
    c: Coincident(g36,g37)
    c: Coincident(g64,g65)
    c: Coincident(g65,g66)
    c: Coincident(g38,g39)
    c: Coincident(g39,g40)
    c: Coincident(g33,g34)
    c: Coincident(g32,g33)
    c: Coincident(g41,g42)
    c: Coincident(g40,g41)
    c: Coincident(g42,g43)
    c: Coincident(g43,g44)
    c: Coincident(g31,g32)
    c: Coincident(g44,g45)
    c: Coincident(g45,g46)
    c: Coincident(g46,g47)
    c: Coincident(g30,g31)
    c: Coincident(g47,g48)
    c: Coincident(g59,g62)
    c: Coincident(g61,g62)
    c: Coincident(g68,g71)
    c: Coincident(g70,g71)
    c: Coincident(g29,g30)
    c: Coincident(g28,g29)
    c: Coincident(g27,g28)
    c: Coincident(g26,g27)
    c: Coincident(g2,g48)
    c: Coincident(g0,g2)
    c: Coincident(g22,g23)
    c: Coincident(g23,g24)
    c: Coincident(g0,g1)
    c: Coincident(g21,g22)
    c: Coincident(g24,g25)
    c: Coincident(g25,g26)
    c: Coincident(g53,g54)
    c: Coincident(g52,g53)
    c: Coincident(g68,g69)
    c: Coincident(g69,g70)
    c: Coincident(g55,g56)
    c: Coincident(g54,g55)
    c: Coincident(g50,g51)
    c: Coincident(g51,g52)
    c: Coincident(g1,g3)
    c: Coincident(g50,g58)
    c: Coincident(g4,g5)
    c: Coincident(g3,g4)
    c: Coincident(g59,g60)
    c: Coincident(g60,g61)
    c: Coincident(g56,g57)
    c: Coincident(g57,g58)
    c: Coincident(g17,g18)
    c: Coincident(g16,g17)
    c: Coincident(g20,g21)
    c: Coincident(g19,g20)
    c: Coincident(g18,g19)
    c: Coincident(g5,g6)
    c: Coincident(g14,g15)
    c: Coincident(g15,g16)
    c: Coincident(g7,g8)
    c: Coincident(g6,g7)
    c: Coincident(g13,g14)
    c: Coincident(g12,g13)
    c: Coincident(g8,g9)
    c: Coincident(g11,g12)
    c: Coincident(g10,g11)
    c: Coincident(g9,g10)
    c: Block(g0)
    c: Block(g1)
    c: Block(g2)
    c: Block(g3)
    c: Block(g4)
    c: Block(g5)
    c: Block(g6)
    c: Block(g7)
    c: Block(g8)
    c: Block(g9)
    c: Block(g10)
    c: Block(g11)
    c: Block(g12)
    c: Block(g13)
    c: Block(g14)
    c: Block(g15)
    c: Block(g16)
    c: Block(g17)
    c: Block(g18)
    c: Block(g19)
    c: Block(g20)
    c: Block(g21)
    c: Block(g22)
    c: Block(g23)
    c: Block(g24)
    c: Block(g25)
    c: Block(g26)
    c: Block(g27)
    c: Block(g28)
    c: Block(g29)
    c: Block(g30)
    c: Block(g31)
    c: Block(g32)
    c: Block(g33)
    c: Block(g34)
    c: Block(g35)
    c: Block(g36)
    c: Block(g37)
    c: Block(g38)
    c: Block(g39)
    c: Block(g40)
    c: Block(g41)
    c: Block(g42)
    c: Block(g43)
    c: Block(g44)
    c: Block(g45)
    c: Block(g46)
    c: Block(g47)
    c: Block(g48)
    c: Block(g49)
    c: Block(g50)
    c: Block(g51)
    c: Block(g52)
    c: Block(g53)
    c: Block(g54)
    c: Block(g55)
    c: Block(g56)
    c: Block(g57)
    c: Block(g58)
    c: Block(g59)
    c: Block(g60)
    c: Block(g61)
    c: Block(g62)
    c: Block(g63)
    c: Block(g64)
    c: Block(g65)
    c: Block(g66)
    c: Block(g67)
    c: Block(g68)
    c: Block(g69)
    c: Block(g70)
    c: Block(g71)
    c: Block(g72)
    c: Block(g73)
    c: Diameter(g75) = 2.4
    c: Coincident(g75,g74)
    c: Equal(g75,g74)
    c: Coincident(g76,g72)
    c: Equal(g76,g72)
    c: Coincident(g77,g49)
    c: Equal(g77,g49)
    c: Diameter(g78) = 2.4
    c: Coincident(g78,g63)
FEATURE [PartDesign::Pocket] Pocket010
  BaseFeature = -> Pocket009
  Direction = (0,0,-1)
  Length = 20
  Length2 = 5
  Profile = -> Sketch025
  ReferenceAxis = -> Sketch025 [N_Axis]
  Refine = true
  Suppressed = false
  Type = 0
FEATURE [PartDesign::Fillet] Fillet
  Base = -> Pocket010 [Edge102,Edge95,Edge85]
  BaseFeature = -> Pocket010
  Radius = 1
  Refine = true
  SupportTransform = false
  Suppressed = false
  UseAllEdges = false
FEATURE [PartDesign::Fillet] Fillet002
  Base = -> Fillet [Edge157,Edge179,Edge180,Edge175,Edge165,Edge168,Edge164,Edge57]
  BaseFeature = -> Fillet
  Radius = 0.499
  Refine = true
  SupportTransform = false
  Suppressed = false
  UseAllEdges = false
FEATURE [Sketcher::SketchObject] Sketch027
  ArcFitTolerance = 1e-06
  AttachmentOffset = pos=(0,0,-5.9) rot=(0,0,1;0rad)
  AttachmentSupport = -> [XY_Plane004]
  FullyConstrained = false
  MakeInternals = false
  MapMode = 5
  Placement = pos=(0,0,-5.9) rot=(0,0,1;0rad)
  expr: Constraints[144] = Sketch025.Constraints[144]
  expr: Constraints[151] = Sketch025.Constraints[151]
  sketch-geometry (83):
    g0: ArcOfCircle [constr] CenterX=45.3 CenterY=2.4 CenterZ=0 NormalX=-1e-16 NormalY=0 NormalZ=1 AngleXU=1.5708 Radius=1.5 StartAngle=0 EndAngle=1.22777
    g1: LineSegment [constr] StartX=59.4 StartY=3.9 StartZ=0 EndX=45.3 EndY=3.9 EndZ=0
    g2: LineSegment [constr] StartX=43.8874 StartY=2.9045 StartZ=0 EndX=43.8874 EndY=2.8 EndZ=0
    g3: ArcOfCircle [constr] CenterX=59.4 CenterY=2.4 CenterZ=0 NormalX=-1e-16 NormalY=0 NormalZ=1 AngleXU=3.90995e-07 Radius=1.5 StartAngle=0 EndAngle=1.5708
    g4: LineSegment [constr] StartX=60.9 StartY=-0.4 StartZ=0 EndX=60.9 EndY=2.4 EndZ=0
    g5: LineSegment [constr] StartX=76.4 StartY=-0.4 StartZ=0 EndX=60.9 EndY=-0.4 EndZ=0
    g6: ArcOfCircle [constr] CenterX=76.4 CenterY=-1.9 CenterZ=0 NormalX=-1e-16 NormalY=0 NormalZ=1 AngleXU=3.90995e-07 Radius=1.5 StartAngle=0 EndAngle=1.5708
    g7: LineSegment [constr] StartX=77.9 StartY=-6.3 StartZ=0 EndX=77.9 EndY=-1.9 EndZ=0
    g8: LineSegment [constr] StartX=96.4 StartY=-6.3 StartZ=0 EndX=77.9 EndY=-6.3 EndZ=0
    g9: ArcOfCircle [constr] CenterX=96.4 CenterY=-7.8 CenterZ=0 NormalX=-1e-16 NormalY=0 NormalZ=1 AngleXU=3.90995e-07 Radius=1.5 StartAngle=0 EndAngle=1.5708
    g10: LineSegment [constr] StartX=97.9 StartY=-59.8 StartZ=0 EndX=97.9 EndY=-7.8 EndZ=0
    g11: LineSegment [constr] StartX=97.9 StartY=-72.8 StartZ=0 EndX=97.9 EndY=-59.8 EndZ=0
    g12: ArcOfCircle [constr] CenterX=96.4 CenterY=-72.8 CenterZ=0 NormalX=-1e-16 NormalY=0 NormalZ=1 AngleXU=-1.5708 Radius=1.5 StartAngle=0 EndAngle=1.5708
    g13: LineSegment [constr] StartX=78 StartY=-74.3 StartZ=0 EndX=96.4 EndY=-74.3 EndZ=0
    g14: ArcOfCircle [constr] CenterX=78 CenterY=-72.8 CenterZ=0 NormalX=-1e-16 NormalY=0 NormalZ=1 AngleXU=-3.14159 Radius=1.5 StartAngle=0 EndAngle=1.5708
    g15: LineSegment [constr] StartX=76.5 StartY=-68.4 StartZ=0 EndX=76.5 EndY=-72.8 EndZ=0
    g16: LineSegment [constr] StartX=68.6 StartY=-68.4 StartZ=0 EndX=76.5 EndY=-68.4 EndZ=0
    g17: LineSegment [constr] StartX=68.6 StartY=-69.9 StartZ=0 EndX=68.6 EndY=-68.4 EndZ=0
    g18: LineSegment [constr] StartX=75 StartY=-69.9 StartZ=0 EndX=68.6 EndY=-69.9 EndZ=0
    g19: LineSegment [constr] StartX=75 StartY=-72.8 StartZ=0 EndX=75 EndY=-69.9 EndZ=0
    g20: ArcOfCircle [constr] CenterX=73.5 CenterY=-72.8 CenterZ=0 NormalX=-1e-16 NormalY=0 NormalZ=1 AngleXU=-1.5708 Radius=1.5 StartAngle=0 EndAngle=1.5708
    g21: LineSegment [constr] StartX=46.1 StartY=-74.3 StartZ=0 EndX=73.5 EndY=-74.3 EndZ=0
    g22: ArcOfCircle [constr] CenterX=46.1 CenterY=-72.8 CenterZ=0 NormalX=-1e-16 NormalY=0 NormalZ=1 AngleXU=-3.14159 Radius=1.5 StartAngle=0 EndAngle=1.5708
    g23: LineSegment [constr] StartX=44.6 StartY=-67.6 StartZ=0 EndX=44.6 EndY=-72.8 EndZ=0
    g24: LineSegment [constr] StartX=49.65 StartY=-67.6 StartZ=0 EndX=44.6 EndY=-67.6 EndZ=0
    g25: LineSegment [constr] StartX=49.65 StartY=-66.1 StartZ=0 EndX=49.65 EndY=-67.6 EndZ=0
    g26: LineSegment [constr] StartX=43.1 StartY=-66.1 StartZ=0 EndX=49.65 EndY=-66.1 EndZ=0
    g27: LineSegment [constr] StartX=43.1 StartY=-71.2 StartZ=0 EndX=43.1 EndY=-66.1 EndZ=0
    g28: ArcOfCircle [constr] CenterX=41.6 CenterY=-71.2 CenterZ=0 NormalX=-1e-16 NormalY=0 NormalZ=1 AngleXU=-1.5708 Radius=1.5 StartAngle=0 EndAngle=1.5708
    g29: LineSegment [constr] StartX=41.4 StartY=-72.7 StartZ=0 EndX=41.6 EndY=-72.7 EndZ=0
    g30: LineSegment [constr] StartX=24.227 StartY=-72.7043 StartZ=0 EndX=41.4 EndY=-72.7 EndZ=0
    g31: LineSegment [constr] StartX=6.18739 StartY=-75.9853 StartZ=0 EndX=24.227 EndY=-72.7043 EndZ=0
    g32: LineSegment [constr] StartX=-12.4977 StartY=-82.7894 StartZ=0 EndX=6.18739 EndY=-75.9853 EndZ=0
    g33: ArcOfCircle [constr] CenterX=-13.011 CenterY=-81.3799 CenterZ=0 NormalX=-1e-16 NormalY=0 NormalZ=1 AngleXU=-2.78726 Radius=1.5 StartAngle=0 EndAngle=1.56568
    g34: LineSegment [constr] StartX=-22.1 StartY=-61.1344 StartZ=0 EndX=-14.4178 EndY=-81.9004 EndZ=0
    g35: LineSegment [constr] StartX=-22.1 StartY=0 StartZ=0 EndX=-22.1 EndY=-61.1344 EndZ=0
    g36: LineSegment [constr] StartX=-16.4 StartY=0 StartZ=0 EndX=-22.1 EndY=0 EndZ=0
    g37: LineSegment [constr] StartX=-16.4 StartY=-10.5 StartZ=0 EndX=-16.4 EndY=0 EndZ=0
    g38: LineSegment [constr] StartX=-14.8 StartY=-10.5 StartZ=0 EndX=-16.4 EndY=-10.5 EndZ=0
    g39: LineSegment [constr] StartX=-14.8 StartY=0 StartZ=0 EndX=-14.8 EndY=-10.5 EndZ=0
    g40: LineSegment [constr] StartX=-5 StartY=0 StartZ=0 EndX=-14.8 EndY=0 EndZ=0
    g41: LineSegment [constr] StartX=-5 StartY=-4 StartZ=0 EndX=-5 EndY=0 EndZ=0
    g42: LineSegment [constr] StartX=5 StartY=-4 StartZ=0 EndX=-5 EndY=-4 EndZ=0
    g43: LineSegment [constr] StartX=5 StartY=0 StartZ=0 EndX=5 EndY=-4 EndZ=0
    g44: LineSegment [constr] StartX=9.9 StartY=0 StartZ=0 EndX=5 EndY=0 EndZ=0
    g45: LineSegment [constr] StartX=9.9 StartY=1.3 StartZ=0 EndX=9.9 EndY=0 EndZ=0
    g46: LineSegment [constr] StartX=23.7 StartY=1.3 StartZ=0 EndX=9.9 EndY=1.3 EndZ=0
    g47: ArcOfCircle [constr] CenterX=25.2 CenterY=1.3 CenterZ=0 NormalX=-1e-16 NormalY=0 NormalZ=1 AngleXU=1.5708 Radius=1.5 StartAngle=0 EndAngle=1.5708
    g48: LineSegment [constr] StartX=43.8874 StartY=2.8 StartZ=0 EndX=25.2 EndY=2.8 EndZ=0
    g49: Circle [constr] CenterX=95.6 CenterY=-57.3 CenterZ=0 NormalX=-1e-16 NormalY=0 NormalZ=1 AngleXU=-1.5708 Radius=1.1
    g50: ArcOfCircle [constr] CenterX=60.7 CenterY=-66.9 CenterZ=0 NormalX=-1e-16 NormalY=0 NormalZ=1 AngleXU=-3.14159 Radius=1.5 StartAngle=0 EndAngle=1.5708
    g51: LineSegment [constr] StartX=59.2 StartY=-66.1 StartZ=0 EndX=59.2 EndY=-66.9 EndZ=0
    g52: LineSegment [constr] StartX=51.15 StartY=-66.1 StartZ=0 EndX=59.2 EndY=-66.1 EndZ=0
    g53: LineSegment [constr] StartX=51.15 StartY=-67.6 StartZ=0 EndX=51.15 EndY=-66.1 EndZ=0
    g54: LineSegment [constr] StartX=56.7 StartY=-67.6 StartZ=0 EndX=51.15 EndY=-67.6 EndZ=0
    g55: LineSegment [constr] StartX=56.7 StartY=-69.9 StartZ=0 EndX=56.7 EndY=-67.6 EndZ=0
    g56: LineSegment [constr] StartX=67.1 StartY=-69.9 StartZ=0 EndX=56.7 EndY=-69.9 EndZ=0
    g57: LineSegment [constr] StartX=67.1 StartY=-68.4 StartZ=0 EndX=67.1 EndY=-69.9 EndZ=0
    g58: LineSegment [constr] StartX=60.7 StartY=-68.4 StartZ=0 EndX=67.1 EndY=-68.4 EndZ=0
    g59: LineSegment [constr] StartX=62.7 StartY=-60 StartZ=0 EndX=27.8 EndY=-60 EndZ=0
    g60: LineSegment [constr] StartX=62.7 StartY=-57.6 StartZ=0 EndX=62.7 EndY=-60 EndZ=0
    g61: LineSegment [constr] StartX=27.8 StartY=-57.6 StartZ=0 EndX=62.7 EndY=-57.6 EndZ=0
    g62: LineSegment [constr] StartX=27.8 StartY=-60 StartZ=0 EndX=27.8 EndY=-57.6 EndZ=0
    g63: Circle [constr] CenterX=-14 CenterY=-73.8 CenterZ=0 NormalX=-1e-16 NormalY=0 NormalZ=1 AngleXU=-1.5708 Radius=1.1
    g64: LineSegment [constr] StartX=-14.8 StartY=-64.1 StartZ=0 EndX=-16.4 EndY=-64.1 EndZ=0
    g65: LineSegment [constr] StartX=-14.8 StartY=-54 StartZ=0 EndX=-14.8 EndY=-64.1 EndZ=0
    g66: LineSegment [constr] StartX=-16.4 StartY=-54 StartZ=0 EndX=-14.8 EndY=-54 EndZ=0
    g67: LineSegment [constr] StartX=-16.4 StartY=-64.1 StartZ=0 EndX=-16.4 EndY=-54 EndZ=0
    g68: LineSegment [constr] StartX=52 StartY=-56.2 StartZ=0 EndX=27.8 EndY=-56.2 EndZ=0
    g69: LineSegment [constr] StartX=52 StartY=-53.8 StartZ=0 EndX=52 EndY=-56.2 EndZ=0
    g70: LineSegment [constr] StartX=27.8 StartY=-53.8 StartZ=0 EndX=52 EndY=-53.8 EndZ=0
    g71: LineSegment [constr] StartX=27.8 StartY=-56.2 StartZ=0 EndX=27.8 EndY=-53.8 EndZ=0
    g72: Circle [constr] CenterX=95.6 CenterY=-23.3 CenterZ=0 NormalX=-1e-16 NormalY=0 NormalZ=1 AngleXU=-1.5708 Radius=1.1
    g73: Circle [constr] CenterX=25.9 CenterY=0.6 CenterZ=0 NormalX=-1e-16 NormalY=0 NormalZ=1 AngleXU=-1.5708 Radius=1.1
    g74: Circle [constr] CenterX=25.9 CenterY=0.6 CenterZ=0 NormalX=0 NormalY=0 NormalZ=1 AngleXU=0 Radius=1.2
    g75: Circle [constr] CenterX=25.9 CenterY=0.6 CenterZ=0 NormalX=0 NormalY=0 NormalZ=1 AngleXU=0 Radius=1.2
    g76: Circle [constr] CenterX=95.6 CenterY=-23.3 CenterZ=0 NormalX=0 NormalY=0 NormalZ=1 AngleXU=0 Radius=1.1
    g77: Circle [constr] CenterX=95.6 CenterY=-57.3 CenterZ=0 NormalX=0 NormalY=0 NormalZ=1 AngleXU=0 Radius=1.1
    g78: Circle [constr] CenterX=-14 CenterY=-73.8 CenterZ=0 NormalX=0 NormalY=0 NormalZ=1 AngleXU=0 Radius=1.2
    g79: Circle CenterX=95.6 CenterY=-23.3 CenterZ=0 NormalX=0 NormalY=0 NormalZ=1 AngleXU=0 Radius=2.5
    g80: Circle CenterX=95.6 CenterY=-57.3 CenterZ=0 NormalX=0 NormalY=0 NormalZ=1 AngleXU=0 Radius=2.5
    g81: Circle CenterX=-14 CenterY=-73.8 CenterZ=0 NormalX=0 NormalY=0 NormalZ=1 AngleXU=0 Radius=2.5
    g82: Circle CenterX=25.9 CenterY=0.6 CenterZ=0 NormalX=0 NormalY=0 NormalZ=1 AngleXU=0 Radius=2.5
  constraints (161):
    c: Coincident(g34,g35)
    c: Coincident(g35,g36)
    c: Coincident(g64,g67)
    c: Coincident(g66,g67)
    c: Coincident(g37,g38)
    c: Coincident(g36,g37)
    c: Coincident(g64,g65)
    c: Coincident(g65,g66)
    c: Coincident(g38,g39)
    c: Coincident(g39,g40)
    c: Coincident(g33,g34)
    c: Coincident(g32,g33)
    c: Coincident(g41,g42)
    c: Coincident(g40,g41)
    c: Coincident(g42,g43)
    c: Coincident(g43,g44)
    c: Coincident(g31,g32)
    c: Coincident(g44,g45)
    c: Coincident(g45,g46)
    c: Coincident(g46,g47)
    c: Coincident(g30,g31)
    c: Coincident(g47,g48)
    c: Coincident(g59,g62)
    c: Coincident(g61,g62)
    c: Coincident(g68,g71)
    c: Coincident(g70,g71)
    c: Coincident(g29,g30)
    c: Coincident(g28,g29)
    c: Coincident(g27,g28)
    c: Coincident(g26,g27)
    c: Coincident(g2,g48)
    c: Coincident(g0,g2)
    c: Coincident(g22,g23)
    c: Coincident(g23,g24)
    c: Coincident(g0,g1)
    c: Coincident(g21,g22)
    c: Coincident(g24,g25)
    c: Coincident(g25,g26)
    c: Coincident(g53,g54)
    c: Coincident(g52,g53)
    c: Coincident(g68,g69)
    c: Coincident(g69,g70)
    c: Coincident(g55,g56)
    c: Coincident(g54,g55)
    c: Coincident(g50,g51)
    c: Coincident(g51,g52)
    c: Coincident(g1,g3)
    c: Coincident(g50,g58)
    c: Coincident(g4,g5)
    c: Coincident(g3,g4)
    c: Coincident(g59,g60)
    c: Coincident(g60,g61)
    c: Coincident(g56,g57)
    c: Coincident(g57,g58)
    c: Coincident(g17,g18)
    c: Coincident(g16,g17)
    c: Coincident(g20,g21)
    c: Coincident(g19,g20)
    c: Coincident(g18,g19)
    c: Coincident(g5,g6)
    c: Coincident(g14,g15)
    c: Coincident(g15,g16)
    c: Coincident(g7,g8)
    c: Coincident(g6,g7)
    c: Coincident(g13,g14)
    c: Coincident(g12,g13)
    c: Coincident(g8,g9)
    c: Coincident(g11,g12)
    c: Coincident(g10,g11)
    c: Coincident(g9,g10)
    c: Block(g0)
    c: Block(g1)
    c: Block(g2)
    c: Block(g3)
    c: Block(g4)
    c: Block(g5)
    c: Block(g6)
    c: Block(g7)
    c: Block(g8)
    c: Block(g9)
    c: Block(g10)
    c: Block(g11)
    c: Block(g12)
    c: Block(g13)
    c: Block(g14)
    c: Block(g15)
    c: Block(g16)
    c: Block(g17)
    c: Block(g18)
    c: Block(g19)
    c: Block(g20)
    c: Block(g21)
    c: Block(g22)
    c: Block(g23)
    c: Block(g24)
    c: Block(g25)
    c: Block(g26)
    c: Block(g27)
    c: Block(g28)
    c: Block(g29)
    c: Block(g30)
    c: Block(g31)
    c: Block(g32)
    c: Block(g33)
    c: Block(g34)
    c: Block(g35)
    c: Block(g36)
    c: Block(g37)
    c: Block(g38)
    c: Block(g39)
    c: Block(g40)
    c: Block(g41)
    c: Block(g42)
    c: Block(g43)
    c: Block(g44)
    c: Block(g45)
    c: Block(g46)
    c: Block(g47)
    c: Block(g48)
    c: Block(g49)
    c: Block(g50)
    c: Block(g51)
    c: Block(g52)
    c: Block(g53)
    c: Block(g54)
    c: Block(g55)
    c: Block(g56)
    c: Block(g57)
    c: Block(g58)
    c: Block(g59)
    c: Block(g60)
    c: Block(g61)
    c: Block(g62)
    c: Block(g63)
    c: Block(g64)
    c: Block(g65)
    c: Block(g66)
    c: Block(g67)
    c: Block(g68)
    c: Block(g69)
    c: Block(g70)
    c: Block(g71)
    c: Block(g72)
    c: Block(g73)
    c: Diameter(g75) = 2.4
    c: Coincident(g75,g74)
    c: Equal(g75,g74)
    c: Coincident(g76,g72)
    c: Equal(g76,g72)
    c: Coincident(g77,g49)
    c: Equal(g77,g49)
    c: Diameter(g78) = 2.4
    c: Coincident(g78,g63)
    c: Diameter(g79) = 5
    c: Coincident(g79,g72)
    c: Diameter(g80) = 5
    c: Coincident(g80,g49)
    c: Diameter(g81) = 5
    c: Coincident(g81,g63)
    c: Diameter(g82) = 5
    c: Coincident(g82,g73)
FEATURE [PartDesign::Pocket] Pocket012
  BaseFeature = -> Fillet002
  Direction = (0,0,-1)
  Length = 5
  Length2 = 5
  Profile = -> Sketch027
  ReferenceAxis = -> Sketch027 [N_Axis]
  Refine = true
  Suppressed = false
  Type = 0
FEATURE [Sketcher::SketchObject] Sketch037
  ArcFitTolerance = 1e-06
  AttachmentOffset = pos=(0,0,-5.1) rot=(0,0,1;0rad)
  AttachmentSupport = -> [XY_Plane004]
  FullyConstrained = true
  MakeInternals = false
  MapMode = 5
  Placement = pos=(0,0,-5.1) rot=(0,0,1;0rad)
  sketch-geometry (5):
    g0: LineSegment StartX=-7.5 StartY=-83 StartZ=0 EndX=-10.3191 EndY=-84.0261 EndZ=0
    g1: LineSegment StartX=-10.3191 StartY=-84.0261 StartZ=0 EndX=-10.9689 EndY=-82.2406 EndZ=0
    g2: LineSegment [constr] StartX=-10.9689 StartY=-82.2406 StartZ=0 EndX=-8.14984 EndY=-81.2146 EndZ=0
    g3: LineSegment StartX=-8.14984 StartY=-81.2146 StartZ=0 EndX=-7.5 EndY=-83 EndZ=0
    g4: ArcOfCircle CenterX=-9.55938 CenterY=-81.7276 CenterZ=0 NormalX=0 NormalY=0 NormalZ=1 AngleXU=0 Radius=1.5 StartAngle=0.349066 EndAngle=3.49066
  constraints (15):
    c: Coincident(g0,g1)
    c: Coincident(g1,g2)
    c: Coincident(g2,g3)
    c: Coincident(g3,g0)
    c: Perpendicular(g2,g1)
    c: Perpendicular(g3,g2)
    c: Perpendicular(g3,g0)
    c: Coincident(g4,g2)
    c: Coincident(g4,g1)
    c: PointOnObject(g4,g2)
    c: Distance(g0,g0) = 3
    c: Angle(g-1,g0) = 0.349066
    c: DistanceX(g0,g-1) = 7.5
    c: DistanceY(g0,g-1) = 83
    c: Distance(g3,g3) = 1.9
FEATURE [PartDesign::Pocket] Pocket019
  BaseFeature = -> Pocket012
  Direction = (0,0,-1)
  Length = 5
  Length2 = 2.4
  Profile = -> Sketch037
  ReferenceAxis = -> Sketch037 [N_Axis]
  Refine = true
  Suppressed = false
  Type = 4
FEATURE [PartDesign::Fillet] Fillet009
  Base = -> Pocket019 [Edge78,Edge80]
  BaseFeature = -> Pocket019
  Radius = 1
  Refine = true
  SupportTransform = false
  Suppressed = false
  UseAllEdges = false
FEATURE [PartDesign::Fillet] Fillet003
  Base = -> Fillet009 [Face1,Face40]
  BaseFeature = -> Fillet009
  Radius = 0.299
  Refine = true
  SupportTransform = false
  Suppressed = false
  UseAllEdges = false
FEATURE [PartDesign::Body] Body001  label="case-key"
  AllowCompound = false
  Group = -> [Sketch020,Sketch022,Sketch021,Pad010,Sketch023,Pocket008,Sketch024,Pocket009,Sketch025,Pocket010,Fillet,Fillet002,Sketch027,Pocket012,Sketch037,Pocket019,Fillet009,Fillet003]
  Origin = -> Origin004
  Tip = -> Fillet003
